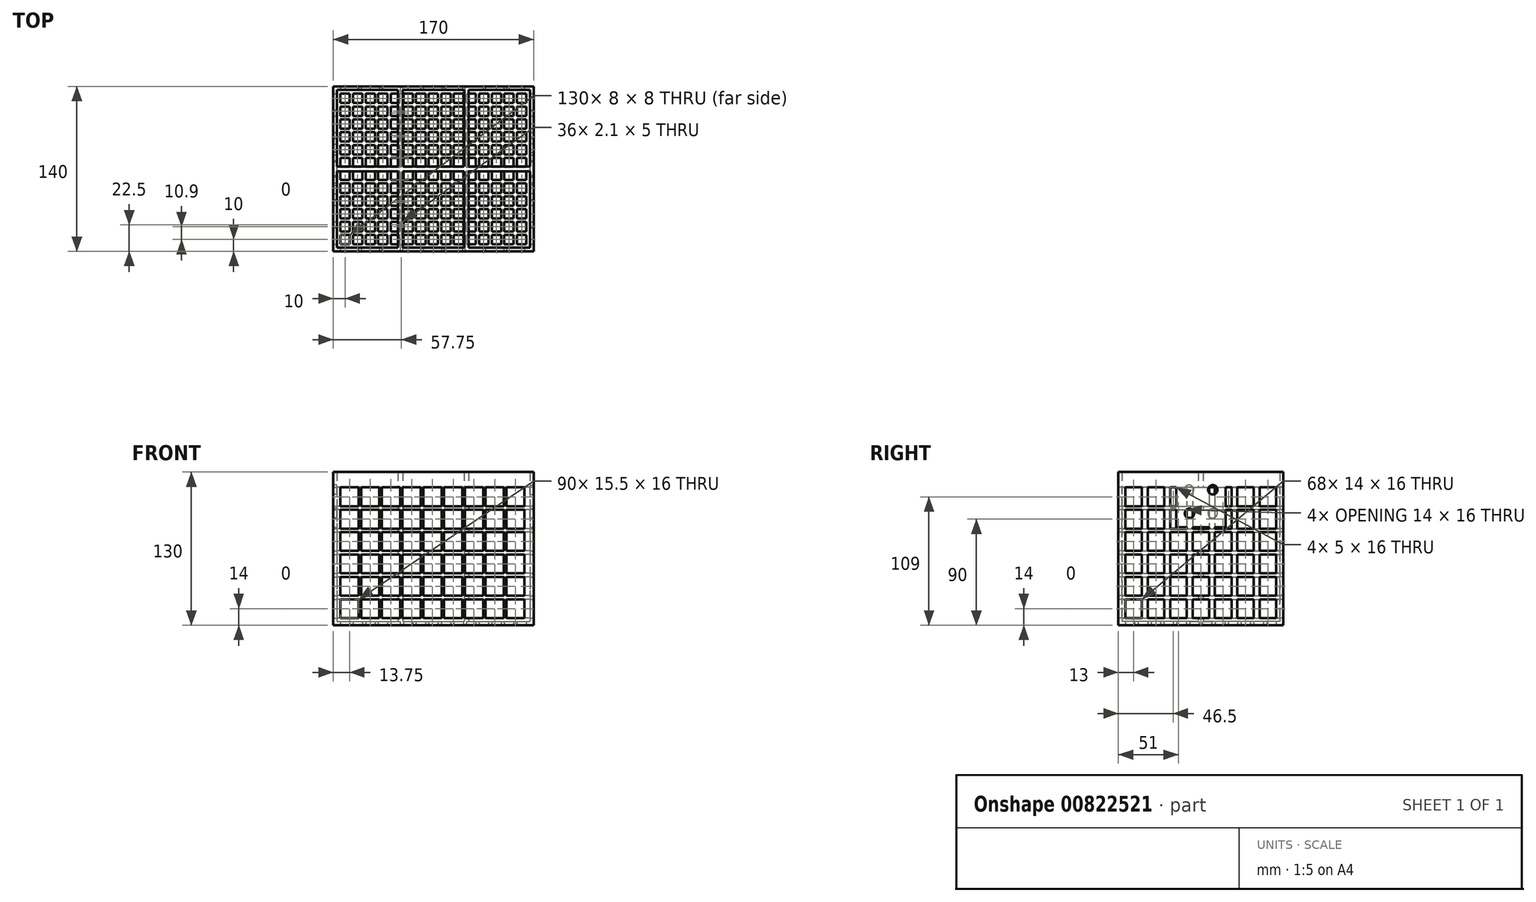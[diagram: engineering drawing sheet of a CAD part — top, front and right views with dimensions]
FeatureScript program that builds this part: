
annotation { "Feature Type Name" : "Feature", "Feature Type Description" : "" }
export const myFeature = defineFeature(function(context is Context, id is Id, definition is map)
    precondition{}
    {
        {
            var Q0;
            Q0=qCreatedBy(makeId("Top.planeOp"),FACE);
            var sketch = newSketch(context, id + "F0", { "sketchPlane" : qUnion([Q0])});
            skLineSegment(sketch, "E0.bottom", {"start": v(0, 0) * mm, "end": v(170, 0) * mm});
            skLineSegment(sketch, "E0.top", {"start": v(0, 140) * mm, "end": v(170, 140) * mm});
            skLineSegment(sketch, "E0.left", {"start": v(0, 0) * mm, "end": v(0, 140) * mm});
            skLineSegment(sketch, "E0.right", {"start": v(170, 0) * mm, "end": v(170, 140) * mm});
            skSolve(sketch);
        }
        {
            var Q0;
            Q0=qSketchRegion(id+"F0",true);
            extrude(context, id + "F1", {"entities" : qUnion([Q0]), "depth" : 130 * mm, "offsetDistance" : 25 * mm});
        }
        {
            var Q0;
            Q0=qCreatedBy(makeId("Top.planeOp"),FACE);
            cPlane(context, id + "F2", {"entities" : qUnion([Q0]), "cplaneType" : CPlaneType.OFFSET, "offset" : 3 * mm, "width" : 150 * mm, "height" : 150 * mm});
        }
        {
            var Q0;
            Q0=qCreatedBy(id+"F2.planeOp",FACE);
            var sketch = newSketch(context, id + "F3", { "sketchPlane" : qUnion([Q0])});
            skLineSegment(sketch, "E1.bottom", {"start": v(3, 68) * mm, "end": v(55, 68) * mm});
            skLineSegment(sketch, "E1.top", {"start": v(3, 3) * mm, "end": v(55, 3) * mm});
            skLineSegment(sketch, "E1.left", {"start": v(3, 68) * mm, "end": v(3, 3) * mm});
            skLineSegment(sketch, "E1.right", {"start": v(55, 68) * mm, "end": v(55, 3) * mm});
            skLineSegment(sketch, "E2", {"start": v(0, 137) * mm, "end": v(173.16, 137) * mm, "construction": true});
            skLineSegment(sketch, "E3", {"start": v(167, 0) * mm, "end": v(167, 146.13) * mm, "construction": true});
            skLineSegment(sketch, "E4.0.1.0", {"start": v(3, 137) * mm, "end": v(55, 137) * mm});
            skLineSegment(sketch, "E4.0.1.1", {"start": v(55, 137) * mm, "end": v(55, 72) * mm});
            skLineSegment(sketch, "E4.0.1.2", {"start": v(3, 72) * mm, "end": v(55, 72) * mm});
            skLineSegment(sketch, "E4.0.1.3", {"start": v(3, 137) * mm, "end": v(3, 72) * mm});
            skLineSegment(sketch, "E4.1.0.0", {"start": v(59, 68) * mm, "end": v(111, 68) * mm});
            skLineSegment(sketch, "E4.1.0.1", {"start": v(111, 68) * mm, "end": v(111, 3) * mm});
            skLineSegment(sketch, "E4.1.0.2", {"start": v(59, 3) * mm, "end": v(111, 3) * mm});
            skLineSegment(sketch, "E4.1.0.3", {"start": v(59, 68) * mm, "end": v(59, 3) * mm});
            skLineSegment(sketch, "E4.1.1.0", {"start": v(59, 137) * mm, "end": v(111, 137) * mm});
            skLineSegment(sketch, "E4.1.1.1", {"start": v(111, 137) * mm, "end": v(111, 72) * mm});
            skLineSegment(sketch, "E4.1.1.2", {"start": v(59, 72) * mm, "end": v(111, 72) * mm});
            skLineSegment(sketch, "E4.1.1.3", {"start": v(59, 137) * mm, "end": v(59, 72) * mm});
            skLineSegment(sketch, "E4.2.0.0", {"start": v(115, 68) * mm, "end": v(167, 68) * mm});
            skLineSegment(sketch, "E4.2.0.1", {"start": v(167, 68) * mm, "end": v(167, 3) * mm});
            skLineSegment(sketch, "E4.2.0.2", {"start": v(115, 3) * mm, "end": v(167, 3) * mm});
            skLineSegment(sketch, "E4.2.0.3", {"start": v(115, 68) * mm, "end": v(115, 3) * mm});
            skLineSegment(sketch, "E4.2.1.0", {"start": v(115, 137) * mm, "end": v(167, 137) * mm});
            skLineSegment(sketch, "E4.2.1.1", {"start": v(167, 137) * mm, "end": v(167, 72) * mm});
            skLineSegment(sketch, "E4.2.1.2", {"start": v(115, 72) * mm, "end": v(167, 72) * mm});
            skLineSegment(sketch, "E4.2.1.3", {"start": v(115, 137) * mm, "end": v(115, 72) * mm});
            skLineSegment(sketch, "E4.direction1", {"start": v(3, 3) * mm, "end": v(59, 3) * mm, "construction": true});
            skLineSegment(sketch, "E4.direction2", {"start": v(3, 3) * mm, "end": v(3, 72) * mm, "construction": true});
            skSolve(sketch);
        }
        {
            var Q0;
            Q0=qSketchRegion(id+"F3",true);
            extrude(context, id + "F4", {"entities" : qUnion([Q0]), "operationType" : NewBodyOperationType.REMOVE, "endBound" : BoundingType.UP_TO_NEXT, "depth" : 25 * mm, "offsetDistance" : 25 * mm});
        }
        {
            var Q0;
            Q0=qCreatedBy(makeId("Top.planeOp"),FACE);
            var sketch = newSketch(context, id + "F5", { "sketchPlane" : qUnion([Q0])});
            skLineSegment(sketch, "E5.bottom", {"start": v(6, 6) * mm, "end": v(14, 6) * mm});
            skLineSegment(sketch, "E5.top", {"start": v(6, 14) * mm, "end": v(14, 14) * mm});
            skLineSegment(sketch, "E5.left", {"start": v(6, 6) * mm, "end": v(6, 14) * mm});
            skLineSegment(sketch, "E5.right", {"start": v(14, 6) * mm, "end": v(14, 14) * mm});
            skLineSegment(sketch, "E6", {"start": v(164, 0) * mm, "end": v(164, 62.65) * mm, "construction": true});
            skLineSegment(sketch, "E7", {"start": v(-7.34, 134) * mm, "end": v(91.38, 134) * mm, "construction": true});
            skLineSegment(sketch, "E8.0.1.0", {"start": v(6, 16.9) * mm, "end": v(14, 16.9) * mm});
            skLineSegment(sketch, "E8.0.1.1", {"start": v(14, 16.9) * mm, "end": v(14, 24.9) * mm});
            skLineSegment(sketch, "E8.0.1.2", {"start": v(6, 24.9) * mm, "end": v(14, 24.9) * mm});
            skLineSegment(sketch, "E8.0.1.3", {"start": v(6, 16.9) * mm, "end": v(6, 24.9) * mm});
            skLineSegment(sketch, "E8.0.2.0", {"start": v(6, 27.8) * mm, "end": v(14, 27.8) * mm});
            skLineSegment(sketch, "E8.0.2.1", {"start": v(14, 27.8) * mm, "end": v(14, 35.8) * mm});
            skLineSegment(sketch, "E8.0.2.2", {"start": v(6, 35.8) * mm, "end": v(14, 35.8) * mm});
            skLineSegment(sketch, "E8.0.2.3", {"start": v(6, 27.8) * mm, "end": v(6, 35.8) * mm});
            skLineSegment(sketch, "E8.0.3.0", {"start": v(6, 38.7) * mm, "end": v(14, 38.7) * mm});
            skLineSegment(sketch, "E8.0.3.1", {"start": v(14, 38.7) * mm, "end": v(14, 46.7) * mm});
            skLineSegment(sketch, "E8.0.3.2", {"start": v(6, 46.7) * mm, "end": v(14, 46.7) * mm});
            skLineSegment(sketch, "E8.0.3.3", {"start": v(6, 38.7) * mm, "end": v(6, 46.7) * mm});
            skLineSegment(sketch, "E8.0.4.0", {"start": v(6, 49.6) * mm, "end": v(14, 49.6) * mm});
            skLineSegment(sketch, "E8.0.4.1", {"start": v(14, 49.6) * mm, "end": v(14, 57.6) * mm});
            skLineSegment(sketch, "E8.0.4.2", {"start": v(6, 57.6) * mm, "end": v(14, 57.6) * mm});
            skLineSegment(sketch, "E8.0.4.3", {"start": v(6, 49.6) * mm, "end": v(6, 57.6) * mm});
            skLineSegment(sketch, "E8.0.5.0", {"start": v(6, 60.5) * mm, "end": v(14, 60.5) * mm});
            skLineSegment(sketch, "E8.0.5.1", {"start": v(14, 60.5) * mm, "end": v(14, 68.5) * mm});
            skLineSegment(sketch, "E8.0.5.2", {"start": v(6, 68.5) * mm, "end": v(14, 68.5) * mm});
            skLineSegment(sketch, "E8.0.5.3", {"start": v(6, 60.5) * mm, "end": v(6, 68.5) * mm});
            skLineSegment(sketch, "E8.0.6.0", {"start": v(6, 71.4) * mm, "end": v(14, 71.4) * mm});
            skLineSegment(sketch, "E8.0.6.1", {"start": v(14, 71.4) * mm, "end": v(14, 79.4) * mm});
            skLineSegment(sketch, "E8.0.6.2", {"start": v(6, 79.4) * mm, "end": v(14, 79.4) * mm});
            skLineSegment(sketch, "E8.0.6.3", {"start": v(6, 71.4) * mm, "end": v(6, 79.4) * mm});
            skLineSegment(sketch, "E8.0.7.0", {"start": v(6, 82.3) * mm, "end": v(14, 82.3) * mm});
            skLineSegment(sketch, "E8.0.7.1", {"start": v(14, 82.3) * mm, "end": v(14, 90.3) * mm});
            skLineSegment(sketch, "E8.0.7.2", {"start": v(6, 90.3) * mm, "end": v(14, 90.3) * mm});
            skLineSegment(sketch, "E8.0.7.3", {"start": v(6, 82.3) * mm, "end": v(6, 90.3) * mm});
            skLineSegment(sketch, "E8.0.8.0", {"start": v(6, 93.2) * mm, "end": v(14, 93.2) * mm});
            skLineSegment(sketch, "E8.0.8.1", {"start": v(14, 93.2) * mm, "end": v(14, 101.2) * mm});
            skLineSegment(sketch, "E8.0.8.2", {"start": v(6, 101.2) * mm, "end": v(14, 101.2) * mm});
            skLineSegment(sketch, "E8.0.8.3", {"start": v(6, 93.2) * mm, "end": v(6, 101.2) * mm});
            skLineSegment(sketch, "E8.0.9.0", {"start": v(6, 104.1) * mm, "end": v(14, 104.1) * mm});
            skLineSegment(sketch, "E8.0.9.1", {"start": v(14, 104.1) * mm, "end": v(14, 112.1) * mm});
            skLineSegment(sketch, "E8.0.9.2", {"start": v(6, 112.1) * mm, "end": v(14, 112.1) * mm});
            skLineSegment(sketch, "E8.0.9.3", {"start": v(6, 104.1) * mm, "end": v(6, 112.1) * mm});
            skLineSegment(sketch, "E8.0.10.0", {"start": v(6, 115) * mm, "end": v(14, 115) * mm});
            skLineSegment(sketch, "E8.0.10.1", {"start": v(14, 115) * mm, "end": v(14, 123) * mm});
            skLineSegment(sketch, "E8.0.10.2", {"start": v(6, 123) * mm, "end": v(14, 123) * mm});
            skLineSegment(sketch, "E8.0.10.3", {"start": v(6, 115) * mm, "end": v(6, 123) * mm});
            skLineSegment(sketch, "E8.0.11.0", {"start": v(6, 125.9) * mm, "end": v(14, 125.9) * mm});
            skLineSegment(sketch, "E8.0.11.1", {"start": v(14, 125.9) * mm, "end": v(14, 133.9) * mm});
            skLineSegment(sketch, "E8.0.11.2", {"start": v(6, 133.9) * mm, "end": v(14, 133.9) * mm});
            skLineSegment(sketch, "E8.0.11.3", {"start": v(6, 125.9) * mm, "end": v(6, 133.9) * mm});
            skLineSegment(sketch, "E8.1.0.0", {"start": v(16.7, 6) * mm, "end": v(24.7, 6) * mm});
            skLineSegment(sketch, "E8.1.0.1", {"start": v(24.7, 6) * mm, "end": v(24.7, 14) * mm});
            skLineSegment(sketch, "E8.1.0.2", {"start": v(16.7, 14) * mm, "end": v(24.7, 14) * mm});
            skLineSegment(sketch, "E8.1.0.3", {"start": v(16.7, 6) * mm, "end": v(16.7, 14) * mm});
            skLineSegment(sketch, "E8.1.1.0", {"start": v(16.7, 16.9) * mm, "end": v(24.7, 16.9) * mm});
            skLineSegment(sketch, "E8.1.1.1", {"start": v(24.7, 16.9) * mm, "end": v(24.7, 24.9) * mm});
            skLineSegment(sketch, "E8.1.1.2", {"start": v(16.7, 24.9) * mm, "end": v(24.7, 24.9) * mm});
            skLineSegment(sketch, "E8.1.1.3", {"start": v(16.7, 16.9) * mm, "end": v(16.7, 24.9) * mm});
            skLineSegment(sketch, "E8.1.2.0", {"start": v(16.7, 27.8) * mm, "end": v(24.7, 27.8) * mm});
            skLineSegment(sketch, "E8.1.2.1", {"start": v(24.7, 27.8) * mm, "end": v(24.7, 35.8) * mm});
            skLineSegment(sketch, "E8.1.2.2", {"start": v(16.7, 35.8) * mm, "end": v(24.7, 35.8) * mm});
            skLineSegment(sketch, "E8.1.2.3", {"start": v(16.7, 27.8) * mm, "end": v(16.7, 35.8) * mm});
            skLineSegment(sketch, "E8.1.3.0", {"start": v(16.7, 38.7) * mm, "end": v(24.7, 38.7) * mm});
            skLineSegment(sketch, "E8.1.3.1", {"start": v(24.7, 38.7) * mm, "end": v(24.7, 46.7) * mm});
            skLineSegment(sketch, "E8.1.3.2", {"start": v(16.7, 46.7) * mm, "end": v(24.7, 46.7) * mm});
            skLineSegment(sketch, "E8.1.3.3", {"start": v(16.7, 38.7) * mm, "end": v(16.7, 46.7) * mm});
            skLineSegment(sketch, "E8.1.4.0", {"start": v(16.7, 49.6) * mm, "end": v(24.7, 49.6) * mm});
            skLineSegment(sketch, "E8.1.4.1", {"start": v(24.7, 49.6) * mm, "end": v(24.7, 57.6) * mm});
            skLineSegment(sketch, "E8.1.4.2", {"start": v(16.7, 57.6) * mm, "end": v(24.7, 57.6) * mm});
            skLineSegment(sketch, "E8.1.4.3", {"start": v(16.7, 49.6) * mm, "end": v(16.7, 57.6) * mm});
            skLineSegment(sketch, "E8.1.5.0", {"start": v(16.7, 60.5) * mm, "end": v(24.7, 60.5) * mm});
            skLineSegment(sketch, "E8.1.5.1", {"start": v(24.7, 60.5) * mm, "end": v(24.7, 68.5) * mm});
            skLineSegment(sketch, "E8.1.5.2", {"start": v(16.7, 68.5) * mm, "end": v(24.7, 68.5) * mm});
            skLineSegment(sketch, "E8.1.5.3", {"start": v(16.7, 60.5) * mm, "end": v(16.7, 68.5) * mm});
            skLineSegment(sketch, "E8.1.6.0", {"start": v(16.7, 71.4) * mm, "end": v(24.7, 71.4) * mm});
            skLineSegment(sketch, "E8.1.6.1", {"start": v(24.7, 71.4) * mm, "end": v(24.7, 79.4) * mm});
            skLineSegment(sketch, "E8.1.6.2", {"start": v(16.7, 79.4) * mm, "end": v(24.7, 79.4) * mm});
            skLineSegment(sketch, "E8.1.6.3", {"start": v(16.7, 71.4) * mm, "end": v(16.7, 79.4) * mm});
            skLineSegment(sketch, "E8.1.7.0", {"start": v(16.7, 82.3) * mm, "end": v(24.7, 82.3) * mm});
            skLineSegment(sketch, "E8.1.7.1", {"start": v(24.7, 82.3) * mm, "end": v(24.7, 90.3) * mm});
            skLineSegment(sketch, "E8.1.7.2", {"start": v(16.7, 90.3) * mm, "end": v(24.7, 90.3) * mm});
            skLineSegment(sketch, "E8.1.7.3", {"start": v(16.7, 82.3) * mm, "end": v(16.7, 90.3) * mm});
            skLineSegment(sketch, "E8.1.8.0", {"start": v(16.7, 93.2) * mm, "end": v(24.7, 93.2) * mm});
            skLineSegment(sketch, "E8.1.8.1", {"start": v(24.7, 93.2) * mm, "end": v(24.7, 101.2) * mm});
            skLineSegment(sketch, "E8.1.8.2", {"start": v(16.7, 101.2) * mm, "end": v(24.7, 101.2) * mm});
            skLineSegment(sketch, "E8.1.8.3", {"start": v(16.7, 93.2) * mm, "end": v(16.7, 101.2) * mm});
            skLineSegment(sketch, "E8.1.9.0", {"start": v(16.7, 104.1) * mm, "end": v(24.7, 104.1) * mm});
            skLineSegment(sketch, "E8.1.9.1", {"start": v(24.7, 104.1) * mm, "end": v(24.7, 112.1) * mm});
            skLineSegment(sketch, "E8.1.9.2", {"start": v(16.7, 112.1) * mm, "end": v(24.7, 112.1) * mm});
            skLineSegment(sketch, "E8.1.9.3", {"start": v(16.7, 104.1) * mm, "end": v(16.7, 112.1) * mm});
            skLineSegment(sketch, "E8.1.10.0", {"start": v(16.7, 115) * mm, "end": v(24.7, 115) * mm});
            skLineSegment(sketch, "E8.1.10.1", {"start": v(24.7, 115) * mm, "end": v(24.7, 123) * mm});
            skLineSegment(sketch, "E8.1.10.2", {"start": v(16.7, 123) * mm, "end": v(24.7, 123) * mm});
            skLineSegment(sketch, "E8.1.10.3", {"start": v(16.7, 115) * mm, "end": v(16.7, 123) * mm});
            skLineSegment(sketch, "E8.1.11.0", {"start": v(16.7, 125.9) * mm, "end": v(24.7, 125.9) * mm});
            skLineSegment(sketch, "E8.1.11.1", {"start": v(24.7, 125.9) * mm, "end": v(24.7, 133.9) * mm});
            skLineSegment(sketch, "E8.1.11.2", {"start": v(16.7, 133.9) * mm, "end": v(24.7, 133.9) * mm});
            skLineSegment(sketch, "E8.1.11.3", {"start": v(16.7, 125.9) * mm, "end": v(16.7, 133.9) * mm});
            skLineSegment(sketch, "E8.2.0.0", {"start": v(27.4, 6) * mm, "end": v(35.4, 6) * mm});
            skLineSegment(sketch, "E8.2.0.1", {"start": v(35.4, 6) * mm, "end": v(35.4, 14) * mm});
            skLineSegment(sketch, "E8.2.0.2", {"start": v(27.4, 14) * mm, "end": v(35.4, 14) * mm});
            skLineSegment(sketch, "E8.2.0.3", {"start": v(27.4, 6) * mm, "end": v(27.4, 14) * mm});
            skLineSegment(sketch, "E8.2.1.0", {"start": v(27.4, 16.9) * mm, "end": v(35.4, 16.9) * mm});
            skLineSegment(sketch, "E8.2.1.1", {"start": v(35.4, 16.9) * mm, "end": v(35.4, 24.9) * mm});
            skLineSegment(sketch, "E8.2.1.2", {"start": v(27.4, 24.9) * mm, "end": v(35.4, 24.9) * mm});
            skLineSegment(sketch, "E8.2.1.3", {"start": v(27.4, 16.9) * mm, "end": v(27.4, 24.9) * mm});
            skLineSegment(sketch, "E8.2.2.0", {"start": v(27.4, 27.8) * mm, "end": v(35.4, 27.8) * mm});
            skLineSegment(sketch, "E8.2.2.1", {"start": v(35.4, 27.8) * mm, "end": v(35.4, 35.8) * mm});
            skLineSegment(sketch, "E8.2.2.2", {"start": v(27.4, 35.8) * mm, "end": v(35.4, 35.8) * mm});
            skLineSegment(sketch, "E8.2.2.3", {"start": v(27.4, 27.8) * mm, "end": v(27.4, 35.8) * mm});
            skLineSegment(sketch, "E8.2.3.0", {"start": v(27.4, 38.7) * mm, "end": v(35.4, 38.7) * mm});
            skLineSegment(sketch, "E8.2.3.1", {"start": v(35.4, 38.7) * mm, "end": v(35.4, 46.7) * mm});
            skLineSegment(sketch, "E8.2.3.2", {"start": v(27.4, 46.7) * mm, "end": v(35.4, 46.7) * mm});
            skLineSegment(sketch, "E8.2.3.3", {"start": v(27.4, 38.7) * mm, "end": v(27.4, 46.7) * mm});
            skLineSegment(sketch, "E8.2.4.0", {"start": v(27.4, 49.6) * mm, "end": v(35.4, 49.6) * mm});
            skLineSegment(sketch, "E8.2.4.1", {"start": v(35.4, 49.6) * mm, "end": v(35.4, 57.6) * mm});
            skLineSegment(sketch, "E8.2.4.2", {"start": v(27.4, 57.6) * mm, "end": v(35.4, 57.6) * mm});
            skLineSegment(sketch, "E8.2.4.3", {"start": v(27.4, 49.6) * mm, "end": v(27.4, 57.6) * mm});
            skLineSegment(sketch, "E8.2.5.0", {"start": v(27.4, 60.5) * mm, "end": v(35.4, 60.5) * mm});
            skLineSegment(sketch, "E8.2.5.1", {"start": v(35.4, 60.5) * mm, "end": v(35.4, 68.5) * mm});
            skLineSegment(sketch, "E8.2.5.2", {"start": v(27.4, 68.5) * mm, "end": v(35.4, 68.5) * mm});
            skLineSegment(sketch, "E8.2.5.3", {"start": v(27.4, 60.5) * mm, "end": v(27.4, 68.5) * mm});
            skLineSegment(sketch, "E8.2.6.0", {"start": v(27.4, 71.4) * mm, "end": v(35.4, 71.4) * mm});
            skLineSegment(sketch, "E8.2.6.1", {"start": v(35.4, 71.4) * mm, "end": v(35.4, 79.4) * mm});
            skLineSegment(sketch, "E8.2.6.2", {"start": v(27.4, 79.4) * mm, "end": v(35.4, 79.4) * mm});
            skLineSegment(sketch, "E8.2.6.3", {"start": v(27.4, 71.4) * mm, "end": v(27.4, 79.4) * mm});
            skLineSegment(sketch, "E8.2.7.0", {"start": v(27.4, 82.3) * mm, "end": v(35.4, 82.3) * mm});
            skLineSegment(sketch, "E8.2.7.1", {"start": v(35.4, 82.3) * mm, "end": v(35.4, 90.3) * mm});
            skLineSegment(sketch, "E8.2.7.2", {"start": v(27.4, 90.3) * mm, "end": v(35.4, 90.3) * mm});
            skLineSegment(sketch, "E8.2.7.3", {"start": v(27.4, 82.3) * mm, "end": v(27.4, 90.3) * mm});
            skLineSegment(sketch, "E8.2.8.0", {"start": v(27.4, 93.2) * mm, "end": v(35.4, 93.2) * mm});
            skLineSegment(sketch, "E8.2.8.1", {"start": v(35.4, 93.2) * mm, "end": v(35.4, 101.2) * mm});
            skLineSegment(sketch, "E8.2.8.2", {"start": v(27.4, 101.2) * mm, "end": v(35.4, 101.2) * mm});
            skLineSegment(sketch, "E8.2.8.3", {"start": v(27.4, 93.2) * mm, "end": v(27.4, 101.2) * mm});
            skLineSegment(sketch, "E8.2.9.0", {"start": v(27.4, 104.1) * mm, "end": v(35.4, 104.1) * mm});
            skLineSegment(sketch, "E8.2.9.1", {"start": v(35.4, 104.1) * mm, "end": v(35.4, 112.1) * mm});
            skLineSegment(sketch, "E8.2.9.2", {"start": v(27.4, 112.1) * mm, "end": v(35.4, 112.1) * mm});
            skLineSegment(sketch, "E8.2.9.3", {"start": v(27.4, 104.1) * mm, "end": v(27.4, 112.1) * mm});
            skLineSegment(sketch, "E8.2.10.0", {"start": v(27.4, 115) * mm, "end": v(35.4, 115) * mm});
            skLineSegment(sketch, "E8.2.10.1", {"start": v(35.4, 115) * mm, "end": v(35.4, 123) * mm});
            skLineSegment(sketch, "E8.2.10.2", {"start": v(27.4, 123) * mm, "end": v(35.4, 123) * mm});
            skLineSegment(sketch, "E8.2.10.3", {"start": v(27.4, 115) * mm, "end": v(27.4, 123) * mm});
            skLineSegment(sketch, "E8.2.11.0", {"start": v(27.4, 125.9) * mm, "end": v(35.4, 125.9) * mm});
            skLineSegment(sketch, "E8.2.11.1", {"start": v(35.4, 125.9) * mm, "end": v(35.4, 133.9) * mm});
            skLineSegment(sketch, "E8.2.11.2", {"start": v(27.4, 133.9) * mm, "end": v(35.4, 133.9) * mm});
            skLineSegment(sketch, "E8.2.11.3", {"start": v(27.4, 125.9) * mm, "end": v(27.4, 133.9) * mm});
            skLineSegment(sketch, "E8.3.0.0", {"start": v(38.1, 6) * mm, "end": v(46.1, 6) * mm});
            skLineSegment(sketch, "E8.3.0.1", {"start": v(46.1, 6) * mm, "end": v(46.1, 14) * mm});
            skLineSegment(sketch, "E8.3.0.2", {"start": v(38.1, 14) * mm, "end": v(46.1, 14) * mm});
            skLineSegment(sketch, "E8.3.0.3", {"start": v(38.1, 6) * mm, "end": v(38.1, 14) * mm});
            skLineSegment(sketch, "E8.3.1.0", {"start": v(38.1, 16.9) * mm, "end": v(46.1, 16.9) * mm});
            skLineSegment(sketch, "E8.3.1.1", {"start": v(46.1, 16.9) * mm, "end": v(46.1, 24.9) * mm});
            skLineSegment(sketch, "E8.3.1.2", {"start": v(38.1, 24.9) * mm, "end": v(46.1, 24.9) * mm});
            skLineSegment(sketch, "E8.3.1.3", {"start": v(38.1, 16.9) * mm, "end": v(38.1, 24.9) * mm});
            skLineSegment(sketch, "E8.3.2.0", {"start": v(38.1, 27.8) * mm, "end": v(46.1, 27.8) * mm});
            skLineSegment(sketch, "E8.3.2.1", {"start": v(46.1, 27.8) * mm, "end": v(46.1, 35.8) * mm});
            skLineSegment(sketch, "E8.3.2.2", {"start": v(38.1, 35.8) * mm, "end": v(46.1, 35.8) * mm});
            skLineSegment(sketch, "E8.3.2.3", {"start": v(38.1, 27.8) * mm, "end": v(38.1, 35.8) * mm});
            skLineSegment(sketch, "E8.3.3.0", {"start": v(38.1, 38.7) * mm, "end": v(46.1, 38.7) * mm});
            skLineSegment(sketch, "E8.3.3.1", {"start": v(46.1, 38.7) * mm, "end": v(46.1, 46.7) * mm});
            skLineSegment(sketch, "E8.3.3.2", {"start": v(38.1, 46.7) * mm, "end": v(46.1, 46.7) * mm});
            skLineSegment(sketch, "E8.3.3.3", {"start": v(38.1, 38.7) * mm, "end": v(38.1, 46.7) * mm});
            skLineSegment(sketch, "E8.3.4.0", {"start": v(38.1, 49.6) * mm, "end": v(46.1, 49.6) * mm});
            skLineSegment(sketch, "E8.3.4.1", {"start": v(46.1, 49.6) * mm, "end": v(46.1, 57.6) * mm});
            skLineSegment(sketch, "E8.3.4.2", {"start": v(38.1, 57.6) * mm, "end": v(46.1, 57.6) * mm});
            skLineSegment(sketch, "E8.3.4.3", {"start": v(38.1, 49.6) * mm, "end": v(38.1, 57.6) * mm});
            skLineSegment(sketch, "E8.3.5.0", {"start": v(38.1, 60.5) * mm, "end": v(46.1, 60.5) * mm});
            skLineSegment(sketch, "E8.3.5.1", {"start": v(46.1, 60.5) * mm, "end": v(46.1, 68.5) * mm});
            skLineSegment(sketch, "E8.3.5.2", {"start": v(38.1, 68.5) * mm, "end": v(46.1, 68.5) * mm});
            skLineSegment(sketch, "E8.3.5.3", {"start": v(38.1, 60.5) * mm, "end": v(38.1, 68.5) * mm});
            skLineSegment(sketch, "E8.3.6.0", {"start": v(38.1, 71.4) * mm, "end": v(46.1, 71.4) * mm});
            skLineSegment(sketch, "E8.3.6.1", {"start": v(46.1, 71.4) * mm, "end": v(46.1, 79.4) * mm});
            skLineSegment(sketch, "E8.3.6.2", {"start": v(38.1, 79.4) * mm, "end": v(46.1, 79.4) * mm});
            skLineSegment(sketch, "E8.3.6.3", {"start": v(38.1, 71.4) * mm, "end": v(38.1, 79.4) * mm});
            skLineSegment(sketch, "E8.3.7.0", {"start": v(38.1, 82.3) * mm, "end": v(46.1, 82.3) * mm});
            skLineSegment(sketch, "E8.3.7.1", {"start": v(46.1, 82.3) * mm, "end": v(46.1, 90.3) * mm});
            skLineSegment(sketch, "E8.3.7.2", {"start": v(38.1, 90.3) * mm, "end": v(46.1, 90.3) * mm});
            skLineSegment(sketch, "E8.3.7.3", {"start": v(38.1, 82.3) * mm, "end": v(38.1, 90.3) * mm});
            skLineSegment(sketch, "E8.3.8.0", {"start": v(38.1, 93.2) * mm, "end": v(46.1, 93.2) * mm});
            skLineSegment(sketch, "E8.3.8.1", {"start": v(46.1, 93.2) * mm, "end": v(46.1, 101.2) * mm});
            skLineSegment(sketch, "E8.3.8.2", {"start": v(38.1, 101.2) * mm, "end": v(46.1, 101.2) * mm});
            skLineSegment(sketch, "E8.3.8.3", {"start": v(38.1, 93.2) * mm, "end": v(38.1, 101.2) * mm});
            skLineSegment(sketch, "E8.3.9.0", {"start": v(38.1, 104.1) * mm, "end": v(46.1, 104.1) * mm});
            skLineSegment(sketch, "E8.3.9.1", {"start": v(46.1, 104.1) * mm, "end": v(46.1, 112.1) * mm});
            skLineSegment(sketch, "E8.3.9.2", {"start": v(38.1, 112.1) * mm, "end": v(46.1, 112.1) * mm});
            skLineSegment(sketch, "E8.3.9.3", {"start": v(38.1, 104.1) * mm, "end": v(38.1, 112.1) * mm});
            skLineSegment(sketch, "E8.3.10.0", {"start": v(38.1, 115) * mm, "end": v(46.1, 115) * mm});
            skLineSegment(sketch, "E8.3.10.1", {"start": v(46.1, 115) * mm, "end": v(46.1, 123) * mm});
            skLineSegment(sketch, "E8.3.10.2", {"start": v(38.1, 123) * mm, "end": v(46.1, 123) * mm});
            skLineSegment(sketch, "E8.3.10.3", {"start": v(38.1, 115) * mm, "end": v(38.1, 123) * mm});
            skLineSegment(sketch, "E8.3.11.0", {"start": v(38.1, 125.9) * mm, "end": v(46.1, 125.9) * mm});
            skLineSegment(sketch, "E8.3.11.1", {"start": v(46.1, 125.9) * mm, "end": v(46.1, 133.9) * mm});
            skLineSegment(sketch, "E8.3.11.2", {"start": v(38.1, 133.9) * mm, "end": v(46.1, 133.9) * mm});
            skLineSegment(sketch, "E8.3.11.3", {"start": v(38.1, 125.9) * mm, "end": v(38.1, 133.9) * mm});
            skLineSegment(sketch, "E8.4.0.0", {"start": v(48.8, 6) * mm, "end": v(56.8, 6) * mm});
            skLineSegment(sketch, "E8.4.0.1", {"start": v(56.8, 6) * mm, "end": v(56.8, 14) * mm});
            skLineSegment(sketch, "E8.4.0.2", {"start": v(48.8, 14) * mm, "end": v(56.8, 14) * mm});
            skLineSegment(sketch, "E8.4.0.3", {"start": v(48.8, 6) * mm, "end": v(48.8, 14) * mm});
            skLineSegment(sketch, "E8.4.1.0", {"start": v(48.8, 16.9) * mm, "end": v(56.8, 16.9) * mm});
            skLineSegment(sketch, "E8.4.1.1", {"start": v(56.8, 16.9) * mm, "end": v(56.8, 24.9) * mm});
            skLineSegment(sketch, "E8.4.1.2", {"start": v(48.8, 24.9) * mm, "end": v(56.8, 24.9) * mm});
            skLineSegment(sketch, "E8.4.1.3", {"start": v(48.8, 16.9) * mm, "end": v(48.8, 24.9) * mm});
            skLineSegment(sketch, "E8.4.2.0", {"start": v(48.8, 27.8) * mm, "end": v(56.8, 27.8) * mm});
            skLineSegment(sketch, "E8.4.2.1", {"start": v(56.8, 27.8) * mm, "end": v(56.8, 35.8) * mm});
            skLineSegment(sketch, "E8.4.2.2", {"start": v(48.8, 35.8) * mm, "end": v(56.8, 35.8) * mm});
            skLineSegment(sketch, "E8.4.2.3", {"start": v(48.8, 27.8) * mm, "end": v(48.8, 35.8) * mm});
            skLineSegment(sketch, "E8.4.3.0", {"start": v(48.8, 38.7) * mm, "end": v(56.8, 38.7) * mm});
            skLineSegment(sketch, "E8.4.3.1", {"start": v(56.8, 38.7) * mm, "end": v(56.8, 46.7) * mm});
            skLineSegment(sketch, "E8.4.3.2", {"start": v(48.8, 46.7) * mm, "end": v(56.8, 46.7) * mm});
            skLineSegment(sketch, "E8.4.3.3", {"start": v(48.8, 38.7) * mm, "end": v(48.8, 46.7) * mm});
            skLineSegment(sketch, "E8.4.4.0", {"start": v(48.8, 49.6) * mm, "end": v(56.8, 49.6) * mm});
            skLineSegment(sketch, "E8.4.4.1", {"start": v(56.8, 49.6) * mm, "end": v(56.8, 57.6) * mm});
            skLineSegment(sketch, "E8.4.4.2", {"start": v(48.8, 57.6) * mm, "end": v(56.8, 57.6) * mm});
            skLineSegment(sketch, "E8.4.4.3", {"start": v(48.8, 49.6) * mm, "end": v(48.8, 57.6) * mm});
            skLineSegment(sketch, "E8.4.5.0", {"start": v(48.8, 60.5) * mm, "end": v(56.8, 60.5) * mm});
            skLineSegment(sketch, "E8.4.5.1", {"start": v(56.8, 60.5) * mm, "end": v(56.8, 68.5) * mm});
            skLineSegment(sketch, "E8.4.5.2", {"start": v(48.8, 68.5) * mm, "end": v(56.8, 68.5) * mm});
            skLineSegment(sketch, "E8.4.5.3", {"start": v(48.8, 60.5) * mm, "end": v(48.8, 68.5) * mm});
            skLineSegment(sketch, "E8.4.6.0", {"start": v(48.8, 71.4) * mm, "end": v(56.8, 71.4) * mm});
            skLineSegment(sketch, "E8.4.6.1", {"start": v(56.8, 71.4) * mm, "end": v(56.8, 79.4) * mm});
            skLineSegment(sketch, "E8.4.6.2", {"start": v(48.8, 79.4) * mm, "end": v(56.8, 79.4) * mm});
            skLineSegment(sketch, "E8.4.6.3", {"start": v(48.8, 71.4) * mm, "end": v(48.8, 79.4) * mm});
            skLineSegment(sketch, "E8.4.7.0", {"start": v(48.8, 82.3) * mm, "end": v(56.8, 82.3) * mm});
            skLineSegment(sketch, "E8.4.7.1", {"start": v(56.8, 82.3) * mm, "end": v(56.8, 90.3) * mm});
            skLineSegment(sketch, "E8.4.7.2", {"start": v(48.8, 90.3) * mm, "end": v(56.8, 90.3) * mm});
            skLineSegment(sketch, "E8.4.7.3", {"start": v(48.8, 82.3) * mm, "end": v(48.8, 90.3) * mm});
            skLineSegment(sketch, "E8.4.8.0", {"start": v(48.8, 93.2) * mm, "end": v(56.8, 93.2) * mm});
            skLineSegment(sketch, "E8.4.8.1", {"start": v(56.8, 93.2) * mm, "end": v(56.8, 101.2) * mm});
            skLineSegment(sketch, "E8.4.8.2", {"start": v(48.8, 101.2) * mm, "end": v(56.8, 101.2) * mm});
            skLineSegment(sketch, "E8.4.8.3", {"start": v(48.8, 93.2) * mm, "end": v(48.8, 101.2) * mm});
            skLineSegment(sketch, "E8.4.9.0", {"start": v(48.8, 104.1) * mm, "end": v(56.8, 104.1) * mm});
            skLineSegment(sketch, "E8.4.9.1", {"start": v(56.8, 104.1) * mm, "end": v(56.8, 112.1) * mm});
            skLineSegment(sketch, "E8.4.9.2", {"start": v(48.8, 112.1) * mm, "end": v(56.8, 112.1) * mm});
            skLineSegment(sketch, "E8.4.9.3", {"start": v(48.8, 104.1) * mm, "end": v(48.8, 112.1) * mm});
            skLineSegment(sketch, "E8.4.10.0", {"start": v(48.8, 115) * mm, "end": v(56.8, 115) * mm});
            skLineSegment(sketch, "E8.4.10.1", {"start": v(56.8, 115) * mm, "end": v(56.8, 123) * mm});
            skLineSegment(sketch, "E8.4.10.2", {"start": v(48.8, 123) * mm, "end": v(56.8, 123) * mm});
            skLineSegment(sketch, "E8.4.10.3", {"start": v(48.8, 115) * mm, "end": v(48.8, 123) * mm});
            skLineSegment(sketch, "E8.4.11.0", {"start": v(48.8, 125.9) * mm, "end": v(56.8, 125.9) * mm});
            skLineSegment(sketch, "E8.4.11.1", {"start": v(56.8, 125.9) * mm, "end": v(56.8, 133.9) * mm});
            skLineSegment(sketch, "E8.4.11.2", {"start": v(48.8, 133.9) * mm, "end": v(56.8, 133.9) * mm});
            skLineSegment(sketch, "E8.4.11.3", {"start": v(48.8, 125.9) * mm, "end": v(48.8, 133.9) * mm});
            skLineSegment(sketch, "E8.5.0.0", {"start": v(59.5, 6) * mm, "end": v(67.5, 6) * mm});
            skLineSegment(sketch, "E8.5.0.1", {"start": v(67.5, 6) * mm, "end": v(67.5, 14) * mm});
            skLineSegment(sketch, "E8.5.0.2", {"start": v(59.5, 14) * mm, "end": v(67.5, 14) * mm});
            skLineSegment(sketch, "E8.5.0.3", {"start": v(59.5, 6) * mm, "end": v(59.5, 14) * mm});
            skLineSegment(sketch, "E8.5.1.0", {"start": v(59.5, 16.9) * mm, "end": v(67.5, 16.9) * mm});
            skLineSegment(sketch, "E8.5.1.1", {"start": v(67.5, 16.9) * mm, "end": v(67.5, 24.9) * mm});
            skLineSegment(sketch, "E8.5.1.2", {"start": v(59.5, 24.9) * mm, "end": v(67.5, 24.9) * mm});
            skLineSegment(sketch, "E8.5.1.3", {"start": v(59.5, 16.9) * mm, "end": v(59.5, 24.9) * mm});
            skLineSegment(sketch, "E8.5.2.0", {"start": v(59.5, 27.8) * mm, "end": v(67.5, 27.8) * mm});
            skLineSegment(sketch, "E8.5.2.1", {"start": v(67.5, 27.8) * mm, "end": v(67.5, 35.8) * mm});
            skLineSegment(sketch, "E8.5.2.2", {"start": v(59.5, 35.8) * mm, "end": v(67.5, 35.8) * mm});
            skLineSegment(sketch, "E8.5.2.3", {"start": v(59.5, 27.8) * mm, "end": v(59.5, 35.8) * mm});
            skLineSegment(sketch, "E8.5.3.0", {"start": v(59.5, 38.7) * mm, "end": v(67.5, 38.7) * mm});
            skLineSegment(sketch, "E8.5.3.1", {"start": v(67.5, 38.7) * mm, "end": v(67.5, 46.7) * mm});
            skLineSegment(sketch, "E8.5.3.2", {"start": v(59.5, 46.7) * mm, "end": v(67.5, 46.7) * mm});
            skLineSegment(sketch, "E8.5.3.3", {"start": v(59.5, 38.7) * mm, "end": v(59.5, 46.7) * mm});
            skLineSegment(sketch, "E8.5.4.0", {"start": v(59.5, 49.6) * mm, "end": v(67.5, 49.6) * mm});
            skLineSegment(sketch, "E8.5.4.1", {"start": v(67.5, 49.6) * mm, "end": v(67.5, 57.6) * mm});
            skLineSegment(sketch, "E8.5.4.2", {"start": v(59.5, 57.6) * mm, "end": v(67.5, 57.6) * mm});
            skLineSegment(sketch, "E8.5.4.3", {"start": v(59.5, 49.6) * mm, "end": v(59.5, 57.6) * mm});
            skLineSegment(sketch, "E8.5.5.0", {"start": v(59.5, 60.5) * mm, "end": v(67.5, 60.5) * mm});
            skLineSegment(sketch, "E8.5.5.1", {"start": v(67.5, 60.5) * mm, "end": v(67.5, 68.5) * mm});
            skLineSegment(sketch, "E8.5.5.2", {"start": v(59.5, 68.5) * mm, "end": v(67.5, 68.5) * mm});
            skLineSegment(sketch, "E8.5.5.3", {"start": v(59.5, 60.5) * mm, "end": v(59.5, 68.5) * mm});
            skLineSegment(sketch, "E8.5.6.0", {"start": v(59.5, 71.4) * mm, "end": v(67.5, 71.4) * mm});
            skLineSegment(sketch, "E8.5.6.1", {"start": v(67.5, 71.4) * mm, "end": v(67.5, 79.4) * mm});
            skLineSegment(sketch, "E8.5.6.2", {"start": v(59.5, 79.4) * mm, "end": v(67.5, 79.4) * mm});
            skLineSegment(sketch, "E8.5.6.3", {"start": v(59.5, 71.4) * mm, "end": v(59.5, 79.4) * mm});
            skLineSegment(sketch, "E8.5.7.0", {"start": v(59.5, 82.3) * mm, "end": v(67.5, 82.3) * mm});
            skLineSegment(sketch, "E8.5.7.1", {"start": v(67.5, 82.3) * mm, "end": v(67.5, 90.3) * mm});
            skLineSegment(sketch, "E8.5.7.2", {"start": v(59.5, 90.3) * mm, "end": v(67.5, 90.3) * mm});
            skLineSegment(sketch, "E8.5.7.3", {"start": v(59.5, 82.3) * mm, "end": v(59.5, 90.3) * mm});
            skLineSegment(sketch, "E8.5.8.0", {"start": v(59.5, 93.2) * mm, "end": v(67.5, 93.2) * mm});
            skLineSegment(sketch, "E8.5.8.1", {"start": v(67.5, 93.2) * mm, "end": v(67.5, 101.2) * mm});
            skLineSegment(sketch, "E8.5.8.2", {"start": v(59.5, 101.2) * mm, "end": v(67.5, 101.2) * mm});
            skLineSegment(sketch, "E8.5.8.3", {"start": v(59.5, 93.2) * mm, "end": v(59.5, 101.2) * mm});
            skLineSegment(sketch, "E8.5.9.0", {"start": v(59.5, 104.1) * mm, "end": v(67.5, 104.1) * mm});
            skLineSegment(sketch, "E8.5.9.1", {"start": v(67.5, 104.1) * mm, "end": v(67.5, 112.1) * mm});
            skLineSegment(sketch, "E8.5.9.2", {"start": v(59.5, 112.1) * mm, "end": v(67.5, 112.1) * mm});
            skLineSegment(sketch, "E8.5.9.3", {"start": v(59.5, 104.1) * mm, "end": v(59.5, 112.1) * mm});
            skLineSegment(sketch, "E8.5.10.0", {"start": v(59.5, 115) * mm, "end": v(67.5, 115) * mm});
            skLineSegment(sketch, "E8.5.10.1", {"start": v(67.5, 115) * mm, "end": v(67.5, 123) * mm});
            skLineSegment(sketch, "E8.5.10.2", {"start": v(59.5, 123) * mm, "end": v(67.5, 123) * mm});
            skLineSegment(sketch, "E8.5.10.3", {"start": v(59.5, 115) * mm, "end": v(59.5, 123) * mm});
            skLineSegment(sketch, "E8.5.11.0", {"start": v(59.5, 125.9) * mm, "end": v(67.5, 125.9) * mm});
            skLineSegment(sketch, "E8.5.11.1", {"start": v(67.5, 125.9) * mm, "end": v(67.5, 133.9) * mm});
            skLineSegment(sketch, "E8.5.11.2", {"start": v(59.5, 133.9) * mm, "end": v(67.5, 133.9) * mm});
            skLineSegment(sketch, "E8.5.11.3", {"start": v(59.5, 125.9) * mm, "end": v(59.5, 133.9) * mm});
            skLineSegment(sketch, "E8.6.0.0", {"start": v(70.2, 6) * mm, "end": v(78.2, 6) * mm});
            skLineSegment(sketch, "E8.6.0.1", {"start": v(78.2, 6) * mm, "end": v(78.2, 14) * mm});
            skLineSegment(sketch, "E8.6.0.2", {"start": v(70.2, 14) * mm, "end": v(78.2, 14) * mm});
            skLineSegment(sketch, "E8.6.0.3", {"start": v(70.2, 6) * mm, "end": v(70.2, 14) * mm});
            skLineSegment(sketch, "E8.6.1.0", {"start": v(70.2, 16.9) * mm, "end": v(78.2, 16.9) * mm});
            skLineSegment(sketch, "E8.6.1.1", {"start": v(78.2, 16.9) * mm, "end": v(78.2, 24.9) * mm});
            skLineSegment(sketch, "E8.6.1.2", {"start": v(70.2, 24.9) * mm, "end": v(78.2, 24.9) * mm});
            skLineSegment(sketch, "E8.6.1.3", {"start": v(70.2, 16.9) * mm, "end": v(70.2, 24.9) * mm});
            skLineSegment(sketch, "E8.6.2.0", {"start": v(70.2, 27.8) * mm, "end": v(78.2, 27.8) * mm});
            skLineSegment(sketch, "E8.6.2.1", {"start": v(78.2, 27.8) * mm, "end": v(78.2, 35.8) * mm});
            skLineSegment(sketch, "E8.6.2.2", {"start": v(70.2, 35.8) * mm, "end": v(78.2, 35.8) * mm});
            skLineSegment(sketch, "E8.6.2.3", {"start": v(70.2, 27.8) * mm, "end": v(70.2, 35.8) * mm});
            skLineSegment(sketch, "E8.6.3.0", {"start": v(70.2, 38.7) * mm, "end": v(78.2, 38.7) * mm});
            skLineSegment(sketch, "E8.6.3.1", {"start": v(78.2, 38.7) * mm, "end": v(78.2, 46.7) * mm});
            skLineSegment(sketch, "E8.6.3.2", {"start": v(70.2, 46.7) * mm, "end": v(78.2, 46.7) * mm});
            skLineSegment(sketch, "E8.6.3.3", {"start": v(70.2, 38.7) * mm, "end": v(70.2, 46.7) * mm});
            skLineSegment(sketch, "E8.6.4.0", {"start": v(70.2, 49.6) * mm, "end": v(78.2, 49.6) * mm});
            skLineSegment(sketch, "E8.6.4.1", {"start": v(78.2, 49.6) * mm, "end": v(78.2, 57.6) * mm});
            skLineSegment(sketch, "E8.6.4.2", {"start": v(70.2, 57.6) * mm, "end": v(78.2, 57.6) * mm});
            skLineSegment(sketch, "E8.6.4.3", {"start": v(70.2, 49.6) * mm, "end": v(70.2, 57.6) * mm});
            skLineSegment(sketch, "E8.6.5.0", {"start": v(70.2, 60.5) * mm, "end": v(78.2, 60.5) * mm});
            skLineSegment(sketch, "E8.6.5.1", {"start": v(78.2, 60.5) * mm, "end": v(78.2, 68.5) * mm});
            skLineSegment(sketch, "E8.6.5.2", {"start": v(70.2, 68.5) * mm, "end": v(78.2, 68.5) * mm});
            skLineSegment(sketch, "E8.6.5.3", {"start": v(70.2, 60.5) * mm, "end": v(70.2, 68.5) * mm});
            skLineSegment(sketch, "E8.6.6.0", {"start": v(70.2, 71.4) * mm, "end": v(78.2, 71.4) * mm});
            skLineSegment(sketch, "E8.6.6.1", {"start": v(78.2, 71.4) * mm, "end": v(78.2, 79.4) * mm});
            skLineSegment(sketch, "E8.6.6.2", {"start": v(70.2, 79.4) * mm, "end": v(78.2, 79.4) * mm});
            skLineSegment(sketch, "E8.6.6.3", {"start": v(70.2, 71.4) * mm, "end": v(70.2, 79.4) * mm});
            skLineSegment(sketch, "E8.6.7.0", {"start": v(70.2, 82.3) * mm, "end": v(78.2, 82.3) * mm});
            skLineSegment(sketch, "E8.6.7.1", {"start": v(78.2, 82.3) * mm, "end": v(78.2, 90.3) * mm});
            skLineSegment(sketch, "E8.6.7.2", {"start": v(70.2, 90.3) * mm, "end": v(78.2, 90.3) * mm});
            skLineSegment(sketch, "E8.6.7.3", {"start": v(70.2, 82.3) * mm, "end": v(70.2, 90.3) * mm});
            skLineSegment(sketch, "E8.6.8.0", {"start": v(70.2, 93.2) * mm, "end": v(78.2, 93.2) * mm});
            skLineSegment(sketch, "E8.6.8.1", {"start": v(78.2, 93.2) * mm, "end": v(78.2, 101.2) * mm});
            skLineSegment(sketch, "E8.6.8.2", {"start": v(70.2, 101.2) * mm, "end": v(78.2, 101.2) * mm});
            skLineSegment(sketch, "E8.6.8.3", {"start": v(70.2, 93.2) * mm, "end": v(70.2, 101.2) * mm});
            skLineSegment(sketch, "E8.6.9.0", {"start": v(70.2, 104.1) * mm, "end": v(78.2, 104.1) * mm});
            skLineSegment(sketch, "E8.6.9.1", {"start": v(78.2, 104.1) * mm, "end": v(78.2, 112.1) * mm});
            skLineSegment(sketch, "E8.6.9.2", {"start": v(70.2, 112.1) * mm, "end": v(78.2, 112.1) * mm});
            skLineSegment(sketch, "E8.6.9.3", {"start": v(70.2, 104.1) * mm, "end": v(70.2, 112.1) * mm});
            skLineSegment(sketch, "E8.6.10.0", {"start": v(70.2, 115) * mm, "end": v(78.2, 115) * mm});
            skLineSegment(sketch, "E8.6.10.1", {"start": v(78.2, 115) * mm, "end": v(78.2, 123) * mm});
            skLineSegment(sketch, "E8.6.10.2", {"start": v(70.2, 123) * mm, "end": v(78.2, 123) * mm});
            skLineSegment(sketch, "E8.6.10.3", {"start": v(70.2, 115) * mm, "end": v(70.2, 123) * mm});
            skLineSegment(sketch, "E8.6.11.0", {"start": v(70.2, 125.9) * mm, "end": v(78.2, 125.9) * mm});
            skLineSegment(sketch, "E8.6.11.1", {"start": v(78.2, 125.9) * mm, "end": v(78.2, 133.9) * mm});
            skLineSegment(sketch, "E8.6.11.2", {"start": v(70.2, 133.9) * mm, "end": v(78.2, 133.9) * mm});
            skLineSegment(sketch, "E8.6.11.3", {"start": v(70.2, 125.9) * mm, "end": v(70.2, 133.9) * mm});
            skLineSegment(sketch, "E8.7.0.0", {"start": v(80.9, 6) * mm, "end": v(88.9, 6) * mm});
            skLineSegment(sketch, "E8.7.0.1", {"start": v(88.9, 6) * mm, "end": v(88.9, 14) * mm});
            skLineSegment(sketch, "E8.7.0.2", {"start": v(80.9, 14) * mm, "end": v(88.9, 14) * mm});
            skLineSegment(sketch, "E8.7.0.3", {"start": v(80.9, 6) * mm, "end": v(80.9, 14) * mm});
            skLineSegment(sketch, "E8.7.1.0", {"start": v(80.9, 16.9) * mm, "end": v(88.9, 16.9) * mm});
            skLineSegment(sketch, "E8.7.1.1", {"start": v(88.9, 16.9) * mm, "end": v(88.9, 24.9) * mm});
            skLineSegment(sketch, "E8.7.1.2", {"start": v(80.9, 24.9) * mm, "end": v(88.9, 24.9) * mm});
            skLineSegment(sketch, "E8.7.1.3", {"start": v(80.9, 16.9) * mm, "end": v(80.9, 24.9) * mm});
            skLineSegment(sketch, "E8.7.2.0", {"start": v(80.9, 27.8) * mm, "end": v(88.9, 27.8) * mm});
            skLineSegment(sketch, "E8.7.2.1", {"start": v(88.9, 27.8) * mm, "end": v(88.9, 35.8) * mm});
            skLineSegment(sketch, "E8.7.2.2", {"start": v(80.9, 35.8) * mm, "end": v(88.9, 35.8) * mm});
            skLineSegment(sketch, "E8.7.2.3", {"start": v(80.9, 27.8) * mm, "end": v(80.9, 35.8) * mm});
            skLineSegment(sketch, "E8.7.3.0", {"start": v(80.9, 38.7) * mm, "end": v(88.9, 38.7) * mm});
            skLineSegment(sketch, "E8.7.3.1", {"start": v(88.9, 38.7) * mm, "end": v(88.9, 46.7) * mm});
            skLineSegment(sketch, "E8.7.3.2", {"start": v(80.9, 46.7) * mm, "end": v(88.9, 46.7) * mm});
            skLineSegment(sketch, "E8.7.3.3", {"start": v(80.9, 38.7) * mm, "end": v(80.9, 46.7) * mm});
            skLineSegment(sketch, "E8.7.4.0", {"start": v(80.9, 49.6) * mm, "end": v(88.9, 49.6) * mm});
            skLineSegment(sketch, "E8.7.4.1", {"start": v(88.9, 49.6) * mm, "end": v(88.9, 57.6) * mm});
            skLineSegment(sketch, "E8.7.4.2", {"start": v(80.9, 57.6) * mm, "end": v(88.9, 57.6) * mm});
            skLineSegment(sketch, "E8.7.4.3", {"start": v(80.9, 49.6) * mm, "end": v(80.9, 57.6) * mm});
            skLineSegment(sketch, "E8.7.5.0", {"start": v(80.9, 60.5) * mm, "end": v(88.9, 60.5) * mm});
            skLineSegment(sketch, "E8.7.5.1", {"start": v(88.9, 60.5) * mm, "end": v(88.9, 68.5) * mm});
            skLineSegment(sketch, "E8.7.5.2", {"start": v(80.9, 68.5) * mm, "end": v(88.9, 68.5) * mm});
            skLineSegment(sketch, "E8.7.5.3", {"start": v(80.9, 60.5) * mm, "end": v(80.9, 68.5) * mm});
            skLineSegment(sketch, "E8.7.6.0", {"start": v(80.9, 71.4) * mm, "end": v(88.9, 71.4) * mm});
            skLineSegment(sketch, "E8.7.6.1", {"start": v(88.9, 71.4) * mm, "end": v(88.9, 79.4) * mm});
            skLineSegment(sketch, "E8.7.6.2", {"start": v(80.9, 79.4) * mm, "end": v(88.9, 79.4) * mm});
            skLineSegment(sketch, "E8.7.6.3", {"start": v(80.9, 71.4) * mm, "end": v(80.9, 79.4) * mm});
            skLineSegment(sketch, "E8.7.7.0", {"start": v(80.9, 82.3) * mm, "end": v(88.9, 82.3) * mm});
            skLineSegment(sketch, "E8.7.7.1", {"start": v(88.9, 82.3) * mm, "end": v(88.9, 90.3) * mm});
            skLineSegment(sketch, "E8.7.7.2", {"start": v(80.9, 90.3) * mm, "end": v(88.9, 90.3) * mm});
            skLineSegment(sketch, "E8.7.7.3", {"start": v(80.9, 82.3) * mm, "end": v(80.9, 90.3) * mm});
            skLineSegment(sketch, "E8.7.8.0", {"start": v(80.9, 93.2) * mm, "end": v(88.9, 93.2) * mm});
            skLineSegment(sketch, "E8.7.8.1", {"start": v(88.9, 93.2) * mm, "end": v(88.9, 101.2) * mm});
            skLineSegment(sketch, "E8.7.8.2", {"start": v(80.9, 101.2) * mm, "end": v(88.9, 101.2) * mm});
            skLineSegment(sketch, "E8.7.8.3", {"start": v(80.9, 93.2) * mm, "end": v(80.9, 101.2) * mm});
            skLineSegment(sketch, "E8.7.9.0", {"start": v(80.9, 104.1) * mm, "end": v(88.9, 104.1) * mm});
            skLineSegment(sketch, "E8.7.9.1", {"start": v(88.9, 104.1) * mm, "end": v(88.9, 112.1) * mm});
            skLineSegment(sketch, "E8.7.9.2", {"start": v(80.9, 112.1) * mm, "end": v(88.9, 112.1) * mm});
            skLineSegment(sketch, "E8.7.9.3", {"start": v(80.9, 104.1) * mm, "end": v(80.9, 112.1) * mm});
            skLineSegment(sketch, "E8.7.10.0", {"start": v(80.9, 115) * mm, "end": v(88.9, 115) * mm});
            skLineSegment(sketch, "E8.7.10.1", {"start": v(88.9, 115) * mm, "end": v(88.9, 123) * mm});
            skLineSegment(sketch, "E8.7.10.2", {"start": v(80.9, 123) * mm, "end": v(88.9, 123) * mm});
            skLineSegment(sketch, "E8.7.10.3", {"start": v(80.9, 115) * mm, "end": v(80.9, 123) * mm});
            skLineSegment(sketch, "E8.7.11.0", {"start": v(80.9, 125.9) * mm, "end": v(88.9, 125.9) * mm});
            skLineSegment(sketch, "E8.7.11.1", {"start": v(88.9, 125.9) * mm, "end": v(88.9, 133.9) * mm});
            skLineSegment(sketch, "E8.7.11.2", {"start": v(80.9, 133.9) * mm, "end": v(88.9, 133.9) * mm});
            skLineSegment(sketch, "E8.7.11.3", {"start": v(80.9, 125.9) * mm, "end": v(80.9, 133.9) * mm});
            skLineSegment(sketch, "E8.8.0.0", {"start": v(91.6, 6) * mm, "end": v(99.6, 6) * mm});
            skLineSegment(sketch, "E8.8.0.1", {"start": v(99.6, 6) * mm, "end": v(99.6, 14) * mm});
            skLineSegment(sketch, "E8.8.0.2", {"start": v(91.6, 14) * mm, "end": v(99.6, 14) * mm});
            skLineSegment(sketch, "E8.8.0.3", {"start": v(91.6, 6) * mm, "end": v(91.6, 14) * mm});
            skLineSegment(sketch, "E8.8.1.0", {"start": v(91.6, 16.9) * mm, "end": v(99.6, 16.9) * mm});
            skLineSegment(sketch, "E8.8.1.1", {"start": v(99.6, 16.9) * mm, "end": v(99.6, 24.9) * mm});
            skLineSegment(sketch, "E8.8.1.2", {"start": v(91.6, 24.9) * mm, "end": v(99.6, 24.9) * mm});
            skLineSegment(sketch, "E8.8.1.3", {"start": v(91.6, 16.9) * mm, "end": v(91.6, 24.9) * mm});
            skLineSegment(sketch, "E8.8.2.0", {"start": v(91.6, 27.8) * mm, "end": v(99.6, 27.8) * mm});
            skLineSegment(sketch, "E8.8.2.1", {"start": v(99.6, 27.8) * mm, "end": v(99.6, 35.8) * mm});
            skLineSegment(sketch, "E8.8.2.2", {"start": v(91.6, 35.8) * mm, "end": v(99.6, 35.8) * mm});
            skLineSegment(sketch, "E8.8.2.3", {"start": v(91.6, 27.8) * mm, "end": v(91.6, 35.8) * mm});
            skLineSegment(sketch, "E8.8.3.0", {"start": v(91.6, 38.7) * mm, "end": v(99.6, 38.7) * mm});
            skLineSegment(sketch, "E8.8.3.1", {"start": v(99.6, 38.7) * mm, "end": v(99.6, 46.7) * mm});
            skLineSegment(sketch, "E8.8.3.2", {"start": v(91.6, 46.7) * mm, "end": v(99.6, 46.7) * mm});
            skLineSegment(sketch, "E8.8.3.3", {"start": v(91.6, 38.7) * mm, "end": v(91.6, 46.7) * mm});
            skLineSegment(sketch, "E8.8.4.0", {"start": v(91.6, 49.6) * mm, "end": v(99.6, 49.6) * mm});
            skLineSegment(sketch, "E8.8.4.1", {"start": v(99.6, 49.6) * mm, "end": v(99.6, 57.6) * mm});
            skLineSegment(sketch, "E8.8.4.2", {"start": v(91.6, 57.6) * mm, "end": v(99.6, 57.6) * mm});
            skLineSegment(sketch, "E8.8.4.3", {"start": v(91.6, 49.6) * mm, "end": v(91.6, 57.6) * mm});
            skLineSegment(sketch, "E8.8.5.0", {"start": v(91.6, 60.5) * mm, "end": v(99.6, 60.5) * mm});
            skLineSegment(sketch, "E8.8.5.1", {"start": v(99.6, 60.5) * mm, "end": v(99.6, 68.5) * mm});
            skLineSegment(sketch, "E8.8.5.2", {"start": v(91.6, 68.5) * mm, "end": v(99.6, 68.5) * mm});
            skLineSegment(sketch, "E8.8.5.3", {"start": v(91.6, 60.5) * mm, "end": v(91.6, 68.5) * mm});
            skLineSegment(sketch, "E8.8.6.0", {"start": v(91.6, 71.4) * mm, "end": v(99.6, 71.4) * mm});
            skLineSegment(sketch, "E8.8.6.1", {"start": v(99.6, 71.4) * mm, "end": v(99.6, 79.4) * mm});
            skLineSegment(sketch, "E8.8.6.2", {"start": v(91.6, 79.4) * mm, "end": v(99.6, 79.4) * mm});
            skLineSegment(sketch, "E8.8.6.3", {"start": v(91.6, 71.4) * mm, "end": v(91.6, 79.4) * mm});
            skLineSegment(sketch, "E8.8.7.0", {"start": v(91.6, 82.3) * mm, "end": v(99.6, 82.3) * mm});
            skLineSegment(sketch, "E8.8.7.1", {"start": v(99.6, 82.3) * mm, "end": v(99.6, 90.3) * mm});
            skLineSegment(sketch, "E8.8.7.2", {"start": v(91.6, 90.3) * mm, "end": v(99.6, 90.3) * mm});
            skLineSegment(sketch, "E8.8.7.3", {"start": v(91.6, 82.3) * mm, "end": v(91.6, 90.3) * mm});
            skLineSegment(sketch, "E8.8.8.0", {"start": v(91.6, 93.2) * mm, "end": v(99.6, 93.2) * mm});
            skLineSegment(sketch, "E8.8.8.1", {"start": v(99.6, 93.2) * mm, "end": v(99.6, 101.2) * mm});
            skLineSegment(sketch, "E8.8.8.2", {"start": v(91.6, 101.2) * mm, "end": v(99.6, 101.2) * mm});
            skLineSegment(sketch, "E8.8.8.3", {"start": v(91.6, 93.2) * mm, "end": v(91.6, 101.2) * mm});
            skLineSegment(sketch, "E8.8.9.0", {"start": v(91.6, 104.1) * mm, "end": v(99.6, 104.1) * mm});
            skLineSegment(sketch, "E8.8.9.1", {"start": v(99.6, 104.1) * mm, "end": v(99.6, 112.1) * mm});
            skLineSegment(sketch, "E8.8.9.2", {"start": v(91.6, 112.1) * mm, "end": v(99.6, 112.1) * mm});
            skLineSegment(sketch, "E8.8.9.3", {"start": v(91.6, 104.1) * mm, "end": v(91.6, 112.1) * mm});
            skLineSegment(sketch, "E8.8.10.0", {"start": v(91.6, 115) * mm, "end": v(99.6, 115) * mm});
            skLineSegment(sketch, "E8.8.10.1", {"start": v(99.6, 115) * mm, "end": v(99.6, 123) * mm});
            skLineSegment(sketch, "E8.8.10.2", {"start": v(91.6, 123) * mm, "end": v(99.6, 123) * mm});
            skLineSegment(sketch, "E8.8.10.3", {"start": v(91.6, 115) * mm, "end": v(91.6, 123) * mm});
            skLineSegment(sketch, "E8.8.11.0", {"start": v(91.6, 125.9) * mm, "end": v(99.6, 125.9) * mm});
            skLineSegment(sketch, "E8.8.11.1", {"start": v(99.6, 125.9) * mm, "end": v(99.6, 133.9) * mm});
            skLineSegment(sketch, "E8.8.11.2", {"start": v(91.6, 133.9) * mm, "end": v(99.6, 133.9) * mm});
            skLineSegment(sketch, "E8.8.11.3", {"start": v(91.6, 125.9) * mm, "end": v(91.6, 133.9) * mm});
            skLineSegment(sketch, "E8.9.0.0", {"start": v(102.3, 6) * mm, "end": v(110.3, 6) * mm});
            skLineSegment(sketch, "E8.9.0.1", {"start": v(110.3, 6) * mm, "end": v(110.3, 14) * mm});
            skLineSegment(sketch, "E8.9.0.2", {"start": v(102.3, 14) * mm, "end": v(110.3, 14) * mm});
            skLineSegment(sketch, "E8.9.0.3", {"start": v(102.3, 6) * mm, "end": v(102.3, 14) * mm});
            skLineSegment(sketch, "E8.9.1.0", {"start": v(102.3, 16.9) * mm, "end": v(110.3, 16.9) * mm});
            skLineSegment(sketch, "E8.9.1.1", {"start": v(110.3, 16.9) * mm, "end": v(110.3, 24.9) * mm});
            skLineSegment(sketch, "E8.9.1.2", {"start": v(102.3, 24.9) * mm, "end": v(110.3, 24.9) * mm});
            skLineSegment(sketch, "E8.9.1.3", {"start": v(102.3, 16.9) * mm, "end": v(102.3, 24.9) * mm});
            skLineSegment(sketch, "E8.9.2.0", {"start": v(102.3, 27.8) * mm, "end": v(110.3, 27.8) * mm});
            skLineSegment(sketch, "E8.9.2.1", {"start": v(110.3, 27.8) * mm, "end": v(110.3, 35.8) * mm});
            skLineSegment(sketch, "E8.9.2.2", {"start": v(102.3, 35.8) * mm, "end": v(110.3, 35.8) * mm});
            skLineSegment(sketch, "E8.9.2.3", {"start": v(102.3, 27.8) * mm, "end": v(102.3, 35.8) * mm});
            skLineSegment(sketch, "E8.9.3.0", {"start": v(102.3, 38.7) * mm, "end": v(110.3, 38.7) * mm});
            skLineSegment(sketch, "E8.9.3.1", {"start": v(110.3, 38.7) * mm, "end": v(110.3, 46.7) * mm});
            skLineSegment(sketch, "E8.9.3.2", {"start": v(102.3, 46.7) * mm, "end": v(110.3, 46.7) * mm});
            skLineSegment(sketch, "E8.9.3.3", {"start": v(102.3, 38.7) * mm, "end": v(102.3, 46.7) * mm});
            skLineSegment(sketch, "E8.9.4.0", {"start": v(102.3, 49.6) * mm, "end": v(110.3, 49.6) * mm});
            skLineSegment(sketch, "E8.9.4.1", {"start": v(110.3, 49.6) * mm, "end": v(110.3, 57.6) * mm});
            skLineSegment(sketch, "E8.9.4.2", {"start": v(102.3, 57.6) * mm, "end": v(110.3, 57.6) * mm});
            skLineSegment(sketch, "E8.9.4.3", {"start": v(102.3, 49.6) * mm, "end": v(102.3, 57.6) * mm});
            skLineSegment(sketch, "E8.9.5.0", {"start": v(102.3, 60.5) * mm, "end": v(110.3, 60.5) * mm});
            skLineSegment(sketch, "E8.9.5.1", {"start": v(110.3, 60.5) * mm, "end": v(110.3, 68.5) * mm});
            skLineSegment(sketch, "E8.9.5.2", {"start": v(102.3, 68.5) * mm, "end": v(110.3, 68.5) * mm});
            skLineSegment(sketch, "E8.9.5.3", {"start": v(102.3, 60.5) * mm, "end": v(102.3, 68.5) * mm});
            skLineSegment(sketch, "E8.9.6.0", {"start": v(102.3, 71.4) * mm, "end": v(110.3, 71.4) * mm});
            skLineSegment(sketch, "E8.9.6.1", {"start": v(110.3, 71.4) * mm, "end": v(110.3, 79.4) * mm});
            skLineSegment(sketch, "E8.9.6.2", {"start": v(102.3, 79.4) * mm, "end": v(110.3, 79.4) * mm});
            skLineSegment(sketch, "E8.9.6.3", {"start": v(102.3, 71.4) * mm, "end": v(102.3, 79.4) * mm});
            skLineSegment(sketch, "E8.9.7.0", {"start": v(102.3, 82.3) * mm, "end": v(110.3, 82.3) * mm});
            skLineSegment(sketch, "E8.9.7.1", {"start": v(110.3, 82.3) * mm, "end": v(110.3, 90.3) * mm});
            skLineSegment(sketch, "E8.9.7.2", {"start": v(102.3, 90.3) * mm, "end": v(110.3, 90.3) * mm});
            skLineSegment(sketch, "E8.9.7.3", {"start": v(102.3, 82.3) * mm, "end": v(102.3, 90.3) * mm});
            skLineSegment(sketch, "E8.9.8.0", {"start": v(102.3, 93.2) * mm, "end": v(110.3, 93.2) * mm});
            skLineSegment(sketch, "E8.9.8.1", {"start": v(110.3, 93.2) * mm, "end": v(110.3, 101.2) * mm});
            skLineSegment(sketch, "E8.9.8.2", {"start": v(102.3, 101.2) * mm, "end": v(110.3, 101.2) * mm});
            skLineSegment(sketch, "E8.9.8.3", {"start": v(102.3, 93.2) * mm, "end": v(102.3, 101.2) * mm});
            skLineSegment(sketch, "E8.9.9.0", {"start": v(102.3, 104.1) * mm, "end": v(110.3, 104.1) * mm});
            skLineSegment(sketch, "E8.9.9.1", {"start": v(110.3, 104.1) * mm, "end": v(110.3, 112.1) * mm});
            skLineSegment(sketch, "E8.9.9.2", {"start": v(102.3, 112.1) * mm, "end": v(110.3, 112.1) * mm});
            skLineSegment(sketch, "E8.9.9.3", {"start": v(102.3, 104.1) * mm, "end": v(102.3, 112.1) * mm});
            skLineSegment(sketch, "E8.9.10.0", {"start": v(102.3, 115) * mm, "end": v(110.3, 115) * mm});
            skLineSegment(sketch, "E8.9.10.1", {"start": v(110.3, 115) * mm, "end": v(110.3, 123) * mm});
            skLineSegment(sketch, "E8.9.10.2", {"start": v(102.3, 123) * mm, "end": v(110.3, 123) * mm});
            skLineSegment(sketch, "E8.9.10.3", {"start": v(102.3, 115) * mm, "end": v(102.3, 123) * mm});
            skLineSegment(sketch, "E8.9.11.0", {"start": v(102.3, 125.9) * mm, "end": v(110.3, 125.9) * mm});
            skLineSegment(sketch, "E8.9.11.1", {"start": v(110.3, 125.9) * mm, "end": v(110.3, 133.9) * mm});
            skLineSegment(sketch, "E8.9.11.2", {"start": v(102.3, 133.9) * mm, "end": v(110.3, 133.9) * mm});
            skLineSegment(sketch, "E8.9.11.3", {"start": v(102.3, 125.9) * mm, "end": v(102.3, 133.9) * mm});
            skLineSegment(sketch, "E8.10.0.0", {"start": v(113, 6) * mm, "end": v(121, 6) * mm});
            skLineSegment(sketch, "E8.10.0.1", {"start": v(121, 6) * mm, "end": v(121, 14) * mm});
            skLineSegment(sketch, "E8.10.0.2", {"start": v(113, 14) * mm, "end": v(121, 14) * mm});
            skLineSegment(sketch, "E8.10.0.3", {"start": v(113, 6) * mm, "end": v(113, 14) * mm});
            skLineSegment(sketch, "E8.10.1.0", {"start": v(113, 16.9) * mm, "end": v(121, 16.9) * mm});
            skLineSegment(sketch, "E8.10.1.1", {"start": v(121, 16.9) * mm, "end": v(121, 24.9) * mm});
            skLineSegment(sketch, "E8.10.1.2", {"start": v(113, 24.9) * mm, "end": v(121, 24.9) * mm});
            skLineSegment(sketch, "E8.10.1.3", {"start": v(113, 16.9) * mm, "end": v(113, 24.9) * mm});
            skLineSegment(sketch, "E8.10.2.0", {"start": v(113, 27.8) * mm, "end": v(121, 27.8) * mm});
            skLineSegment(sketch, "E8.10.2.1", {"start": v(121, 27.8) * mm, "end": v(121, 35.8) * mm});
            skLineSegment(sketch, "E8.10.2.2", {"start": v(113, 35.8) * mm, "end": v(121, 35.8) * mm});
            skLineSegment(sketch, "E8.10.2.3", {"start": v(113, 27.8) * mm, "end": v(113, 35.8) * mm});
            skLineSegment(sketch, "E8.10.3.0", {"start": v(113, 38.7) * mm, "end": v(121, 38.7) * mm});
            skLineSegment(sketch, "E8.10.3.1", {"start": v(121, 38.7) * mm, "end": v(121, 46.7) * mm});
            skLineSegment(sketch, "E8.10.3.2", {"start": v(113, 46.7) * mm, "end": v(121, 46.7) * mm});
            skLineSegment(sketch, "E8.10.3.3", {"start": v(113, 38.7) * mm, "end": v(113, 46.7) * mm});
            skLineSegment(sketch, "E8.10.4.0", {"start": v(113, 49.6) * mm, "end": v(121, 49.6) * mm});
            skLineSegment(sketch, "E8.10.4.1", {"start": v(121, 49.6) * mm, "end": v(121, 57.6) * mm});
            skLineSegment(sketch, "E8.10.4.2", {"start": v(113, 57.6) * mm, "end": v(121, 57.6) * mm});
            skLineSegment(sketch, "E8.10.4.3", {"start": v(113, 49.6) * mm, "end": v(113, 57.6) * mm});
            skLineSegment(sketch, "E8.10.5.0", {"start": v(113, 60.5) * mm, "end": v(121, 60.5) * mm});
            skLineSegment(sketch, "E8.10.5.1", {"start": v(121, 60.5) * mm, "end": v(121, 68.5) * mm});
            skLineSegment(sketch, "E8.10.5.2", {"start": v(113, 68.5) * mm, "end": v(121, 68.5) * mm});
            skLineSegment(sketch, "E8.10.5.3", {"start": v(113, 60.5) * mm, "end": v(113, 68.5) * mm});
            skLineSegment(sketch, "E8.10.6.0", {"start": v(113, 71.4) * mm, "end": v(121, 71.4) * mm});
            skLineSegment(sketch, "E8.10.6.1", {"start": v(121, 71.4) * mm, "end": v(121, 79.4) * mm});
            skLineSegment(sketch, "E8.10.6.2", {"start": v(113, 79.4) * mm, "end": v(121, 79.4) * mm});
            skLineSegment(sketch, "E8.10.6.3", {"start": v(113, 71.4) * mm, "end": v(113, 79.4) * mm});
            skLineSegment(sketch, "E8.10.7.0", {"start": v(113, 82.3) * mm, "end": v(121, 82.3) * mm});
            skLineSegment(sketch, "E8.10.7.1", {"start": v(121, 82.3) * mm, "end": v(121, 90.3) * mm});
            skLineSegment(sketch, "E8.10.7.2", {"start": v(113, 90.3) * mm, "end": v(121, 90.3) * mm});
            skLineSegment(sketch, "E8.10.7.3", {"start": v(113, 82.3) * mm, "end": v(113, 90.3) * mm});
            skLineSegment(sketch, "E8.10.8.0", {"start": v(113, 93.2) * mm, "end": v(121, 93.2) * mm});
            skLineSegment(sketch, "E8.10.8.1", {"start": v(121, 93.2) * mm, "end": v(121, 101.2) * mm});
            skLineSegment(sketch, "E8.10.8.2", {"start": v(113, 101.2) * mm, "end": v(121, 101.2) * mm});
            skLineSegment(sketch, "E8.10.8.3", {"start": v(113, 93.2) * mm, "end": v(113, 101.2) * mm});
            skLineSegment(sketch, "E8.10.9.0", {"start": v(113, 104.1) * mm, "end": v(121, 104.1) * mm});
            skLineSegment(sketch, "E8.10.9.1", {"start": v(121, 104.1) * mm, "end": v(121, 112.1) * mm});
            skLineSegment(sketch, "E8.10.9.2", {"start": v(113, 112.1) * mm, "end": v(121, 112.1) * mm});
            skLineSegment(sketch, "E8.10.9.3", {"start": v(113, 104.1) * mm, "end": v(113, 112.1) * mm});
            skLineSegment(sketch, "E8.10.10.0", {"start": v(113, 115) * mm, "end": v(121, 115) * mm});
            skLineSegment(sketch, "E8.10.10.1", {"start": v(121, 115) * mm, "end": v(121, 123) * mm});
            skLineSegment(sketch, "E8.10.10.2", {"start": v(113, 123) * mm, "end": v(121, 123) * mm});
            skLineSegment(sketch, "E8.10.10.3", {"start": v(113, 115) * mm, "end": v(113, 123) * mm});
            skLineSegment(sketch, "E8.10.11.0", {"start": v(113, 125.9) * mm, "end": v(121, 125.9) * mm});
            skLineSegment(sketch, "E8.10.11.1", {"start": v(121, 125.9) * mm, "end": v(121, 133.9) * mm});
            skLineSegment(sketch, "E8.10.11.2", {"start": v(113, 133.9) * mm, "end": v(121, 133.9) * mm});
            skLineSegment(sketch, "E8.10.11.3", {"start": v(113, 125.9) * mm, "end": v(113, 133.9) * mm});
            skLineSegment(sketch, "E8.11.0.0", {"start": v(123.7, 6) * mm, "end": v(131.7, 6) * mm});
            skLineSegment(sketch, "E8.11.0.1", {"start": v(131.7, 6) * mm, "end": v(131.7, 14) * mm});
            skLineSegment(sketch, "E8.11.0.2", {"start": v(123.7, 14) * mm, "end": v(131.7, 14) * mm});
            skLineSegment(sketch, "E8.11.0.3", {"start": v(123.7, 6) * mm, "end": v(123.7, 14) * mm});
            skLineSegment(sketch, "E8.11.1.0", {"start": v(123.7, 16.9) * mm, "end": v(131.7, 16.9) * mm});
            skLineSegment(sketch, "E8.11.1.1", {"start": v(131.7, 16.9) * mm, "end": v(131.7, 24.9) * mm});
            skLineSegment(sketch, "E8.11.1.2", {"start": v(123.7, 24.9) * mm, "end": v(131.7, 24.9) * mm});
            skLineSegment(sketch, "E8.11.1.3", {"start": v(123.7, 16.9) * mm, "end": v(123.7, 24.9) * mm});
            skLineSegment(sketch, "E8.11.2.0", {"start": v(123.7, 27.8) * mm, "end": v(131.7, 27.8) * mm});
            skLineSegment(sketch, "E8.11.2.1", {"start": v(131.7, 27.8) * mm, "end": v(131.7, 35.8) * mm});
            skLineSegment(sketch, "E8.11.2.2", {"start": v(123.7, 35.8) * mm, "end": v(131.7, 35.8) * mm});
            skLineSegment(sketch, "E8.11.2.3", {"start": v(123.7, 27.8) * mm, "end": v(123.7, 35.8) * mm});
            skLineSegment(sketch, "E8.11.3.0", {"start": v(123.7, 38.7) * mm, "end": v(131.7, 38.7) * mm});
            skLineSegment(sketch, "E8.11.3.1", {"start": v(131.7, 38.7) * mm, "end": v(131.7, 46.7) * mm});
            skLineSegment(sketch, "E8.11.3.2", {"start": v(123.7, 46.7) * mm, "end": v(131.7, 46.7) * mm});
            skLineSegment(sketch, "E8.11.3.3", {"start": v(123.7, 38.7) * mm, "end": v(123.7, 46.7) * mm});
            skLineSegment(sketch, "E8.11.4.0", {"start": v(123.7, 49.6) * mm, "end": v(131.7, 49.6) * mm});
            skLineSegment(sketch, "E8.11.4.1", {"start": v(131.7, 49.6) * mm, "end": v(131.7, 57.6) * mm});
            skLineSegment(sketch, "E8.11.4.2", {"start": v(123.7, 57.6) * mm, "end": v(131.7, 57.6) * mm});
            skLineSegment(sketch, "E8.11.4.3", {"start": v(123.7, 49.6) * mm, "end": v(123.7, 57.6) * mm});
            skLineSegment(sketch, "E8.11.5.0", {"start": v(123.7, 60.5) * mm, "end": v(131.7, 60.5) * mm});
            skLineSegment(sketch, "E8.11.5.1", {"start": v(131.7, 60.5) * mm, "end": v(131.7, 68.5) * mm});
            skLineSegment(sketch, "E8.11.5.2", {"start": v(123.7, 68.5) * mm, "end": v(131.7, 68.5) * mm});
            skLineSegment(sketch, "E8.11.5.3", {"start": v(123.7, 60.5) * mm, "end": v(123.7, 68.5) * mm});
            skLineSegment(sketch, "E8.11.6.0", {"start": v(123.7, 71.4) * mm, "end": v(131.7, 71.4) * mm});
            skLineSegment(sketch, "E8.11.6.1", {"start": v(131.7, 71.4) * mm, "end": v(131.7, 79.4) * mm});
            skLineSegment(sketch, "E8.11.6.2", {"start": v(123.7, 79.4) * mm, "end": v(131.7, 79.4) * mm});
            skLineSegment(sketch, "E8.11.6.3", {"start": v(123.7, 71.4) * mm, "end": v(123.7, 79.4) * mm});
            skLineSegment(sketch, "E8.11.7.0", {"start": v(123.7, 82.3) * mm, "end": v(131.7, 82.3) * mm});
            skLineSegment(sketch, "E8.11.7.1", {"start": v(131.7, 82.3) * mm, "end": v(131.7, 90.3) * mm});
            skLineSegment(sketch, "E8.11.7.2", {"start": v(123.7, 90.3) * mm, "end": v(131.7, 90.3) * mm});
            skLineSegment(sketch, "E8.11.7.3", {"start": v(123.7, 82.3) * mm, "end": v(123.7, 90.3) * mm});
            skLineSegment(sketch, "E8.11.8.0", {"start": v(123.7, 93.2) * mm, "end": v(131.7, 93.2) * mm});
            skLineSegment(sketch, "E8.11.8.1", {"start": v(131.7, 93.2) * mm, "end": v(131.7, 101.2) * mm});
            skLineSegment(sketch, "E8.11.8.2", {"start": v(123.7, 101.2) * mm, "end": v(131.7, 101.2) * mm});
            skLineSegment(sketch, "E8.11.8.3", {"start": v(123.7, 93.2) * mm, "end": v(123.7, 101.2) * mm});
            skLineSegment(sketch, "E8.11.9.0", {"start": v(123.7, 104.1) * mm, "end": v(131.7, 104.1) * mm});
            skLineSegment(sketch, "E8.11.9.1", {"start": v(131.7, 104.1) * mm, "end": v(131.7, 112.1) * mm});
            skLineSegment(sketch, "E8.11.9.2", {"start": v(123.7, 112.1) * mm, "end": v(131.7, 112.1) * mm});
            skLineSegment(sketch, "E8.11.9.3", {"start": v(123.7, 104.1) * mm, "end": v(123.7, 112.1) * mm});
            skLineSegment(sketch, "E8.11.10.0", {"start": v(123.7, 115) * mm, "end": v(131.7, 115) * mm});
            skLineSegment(sketch, "E8.11.10.1", {"start": v(131.7, 115) * mm, "end": v(131.7, 123) * mm});
            skLineSegment(sketch, "E8.11.10.2", {"start": v(123.7, 123) * mm, "end": v(131.7, 123) * mm});
            skLineSegment(sketch, "E8.11.10.3", {"start": v(123.7, 115) * mm, "end": v(123.7, 123) * mm});
            skLineSegment(sketch, "E8.11.11.0", {"start": v(123.7, 125.9) * mm, "end": v(131.7, 125.9) * mm});
            skLineSegment(sketch, "E8.11.11.1", {"start": v(131.7, 125.9) * mm, "end": v(131.7, 133.9) * mm});
            skLineSegment(sketch, "E8.11.11.2", {"start": v(123.7, 133.9) * mm, "end": v(131.7, 133.9) * mm});
            skLineSegment(sketch, "E8.11.11.3", {"start": v(123.7, 125.9) * mm, "end": v(123.7, 133.9) * mm});
            skLineSegment(sketch, "E8.12.0.0", {"start": v(134.4, 6) * mm, "end": v(142.4, 6) * mm});
            skLineSegment(sketch, "E8.12.0.1", {"start": v(142.4, 6) * mm, "end": v(142.4, 14) * mm});
            skLineSegment(sketch, "E8.12.0.2", {"start": v(134.4, 14) * mm, "end": v(142.4, 14) * mm});
            skLineSegment(sketch, "E8.12.0.3", {"start": v(134.4, 6) * mm, "end": v(134.4, 14) * mm});
            skLineSegment(sketch, "E8.12.1.0", {"start": v(134.4, 16.9) * mm, "end": v(142.4, 16.9) * mm});
            skLineSegment(sketch, "E8.12.1.1", {"start": v(142.4, 16.9) * mm, "end": v(142.4, 24.9) * mm});
            skLineSegment(sketch, "E8.12.1.2", {"start": v(134.4, 24.9) * mm, "end": v(142.4, 24.9) * mm});
            skLineSegment(sketch, "E8.12.1.3", {"start": v(134.4, 16.9) * mm, "end": v(134.4, 24.9) * mm});
            skLineSegment(sketch, "E8.12.2.0", {"start": v(134.4, 27.8) * mm, "end": v(142.4, 27.8) * mm});
            skLineSegment(sketch, "E8.12.2.1", {"start": v(142.4, 27.8) * mm, "end": v(142.4, 35.8) * mm});
            skLineSegment(sketch, "E8.12.2.2", {"start": v(134.4, 35.8) * mm, "end": v(142.4, 35.8) * mm});
            skLineSegment(sketch, "E8.12.2.3", {"start": v(134.4, 27.8) * mm, "end": v(134.4, 35.8) * mm});
            skLineSegment(sketch, "E8.12.3.0", {"start": v(134.4, 38.7) * mm, "end": v(142.4, 38.7) * mm});
            skLineSegment(sketch, "E8.12.3.1", {"start": v(142.4, 38.7) * mm, "end": v(142.4, 46.7) * mm});
            skLineSegment(sketch, "E8.12.3.2", {"start": v(134.4, 46.7) * mm, "end": v(142.4, 46.7) * mm});
            skLineSegment(sketch, "E8.12.3.3", {"start": v(134.4, 38.7) * mm, "end": v(134.4, 46.7) * mm});
            skLineSegment(sketch, "E8.12.4.0", {"start": v(134.4, 49.6) * mm, "end": v(142.4, 49.6) * mm});
            skLineSegment(sketch, "E8.12.4.1", {"start": v(142.4, 49.6) * mm, "end": v(142.4, 57.6) * mm});
            skLineSegment(sketch, "E8.12.4.2", {"start": v(134.4, 57.6) * mm, "end": v(142.4, 57.6) * mm});
            skLineSegment(sketch, "E8.12.4.3", {"start": v(134.4, 49.6) * mm, "end": v(134.4, 57.6) * mm});
            skLineSegment(sketch, "E8.12.5.0", {"start": v(134.4, 60.5) * mm, "end": v(142.4, 60.5) * mm});
            skLineSegment(sketch, "E8.12.5.1", {"start": v(142.4, 60.5) * mm, "end": v(142.4, 68.5) * mm});
            skLineSegment(sketch, "E8.12.5.2", {"start": v(134.4, 68.5) * mm, "end": v(142.4, 68.5) * mm});
            skLineSegment(sketch, "E8.12.5.3", {"start": v(134.4, 60.5) * mm, "end": v(134.4, 68.5) * mm});
            skLineSegment(sketch, "E8.12.6.0", {"start": v(134.4, 71.4) * mm, "end": v(142.4, 71.4) * mm});
            skLineSegment(sketch, "E8.12.6.1", {"start": v(142.4, 71.4) * mm, "end": v(142.4, 79.4) * mm});
            skLineSegment(sketch, "E8.12.6.2", {"start": v(134.4, 79.4) * mm, "end": v(142.4, 79.4) * mm});
            skLineSegment(sketch, "E8.12.6.3", {"start": v(134.4, 71.4) * mm, "end": v(134.4, 79.4) * mm});
            skLineSegment(sketch, "E8.12.7.0", {"start": v(134.4, 82.3) * mm, "end": v(142.4, 82.3) * mm});
            skLineSegment(sketch, "E8.12.7.1", {"start": v(142.4, 82.3) * mm, "end": v(142.4, 90.3) * mm});
            skLineSegment(sketch, "E8.12.7.2", {"start": v(134.4, 90.3) * mm, "end": v(142.4, 90.3) * mm});
            skLineSegment(sketch, "E8.12.7.3", {"start": v(134.4, 82.3) * mm, "end": v(134.4, 90.3) * mm});
            skLineSegment(sketch, "E8.12.8.0", {"start": v(134.4, 93.2) * mm, "end": v(142.4, 93.2) * mm});
            skLineSegment(sketch, "E8.12.8.1", {"start": v(142.4, 93.2) * mm, "end": v(142.4, 101.2) * mm});
            skLineSegment(sketch, "E8.12.8.2", {"start": v(134.4, 101.2) * mm, "end": v(142.4, 101.2) * mm});
            skLineSegment(sketch, "E8.12.8.3", {"start": v(134.4, 93.2) * mm, "end": v(134.4, 101.2) * mm});
            skLineSegment(sketch, "E8.12.9.0", {"start": v(134.4, 104.1) * mm, "end": v(142.4, 104.1) * mm});
            skLineSegment(sketch, "E8.12.9.1", {"start": v(142.4, 104.1) * mm, "end": v(142.4, 112.1) * mm});
            skLineSegment(sketch, "E8.12.9.2", {"start": v(134.4, 112.1) * mm, "end": v(142.4, 112.1) * mm});
            skLineSegment(sketch, "E8.12.9.3", {"start": v(134.4, 104.1) * mm, "end": v(134.4, 112.1) * mm});
            skLineSegment(sketch, "E8.12.10.0", {"start": v(134.4, 115) * mm, "end": v(142.4, 115) * mm});
            skLineSegment(sketch, "E8.12.10.1", {"start": v(142.4, 115) * mm, "end": v(142.4, 123) * mm});
            skLineSegment(sketch, "E8.12.10.2", {"start": v(134.4, 123) * mm, "end": v(142.4, 123) * mm});
            skLineSegment(sketch, "E8.12.10.3", {"start": v(134.4, 115) * mm, "end": v(134.4, 123) * mm});
            skLineSegment(sketch, "E8.12.11.0", {"start": v(134.4, 125.9) * mm, "end": v(142.4, 125.9) * mm});
            skLineSegment(sketch, "E8.12.11.1", {"start": v(142.4, 125.9) * mm, "end": v(142.4, 133.9) * mm});
            skLineSegment(sketch, "E8.12.11.2", {"start": v(134.4, 133.9) * mm, "end": v(142.4, 133.9) * mm});
            skLineSegment(sketch, "E8.12.11.3", {"start": v(134.4, 125.9) * mm, "end": v(134.4, 133.9) * mm});
            skLineSegment(sketch, "E8.13.0.0", {"start": v(145.1, 6) * mm, "end": v(153.1, 6) * mm});
            skLineSegment(sketch, "E8.13.0.1", {"start": v(153.1, 6) * mm, "end": v(153.1, 14) * mm});
            skLineSegment(sketch, "E8.13.0.2", {"start": v(145.1, 14) * mm, "end": v(153.1, 14) * mm});
            skLineSegment(sketch, "E8.13.0.3", {"start": v(145.1, 6) * mm, "end": v(145.1, 14) * mm});
            skLineSegment(sketch, "E8.13.1.0", {"start": v(145.1, 16.9) * mm, "end": v(153.1, 16.9) * mm});
            skLineSegment(sketch, "E8.13.1.1", {"start": v(153.1, 16.9) * mm, "end": v(153.1, 24.9) * mm});
            skLineSegment(sketch, "E8.13.1.2", {"start": v(145.1, 24.9) * mm, "end": v(153.1, 24.9) * mm});
            skLineSegment(sketch, "E8.13.1.3", {"start": v(145.1, 16.9) * mm, "end": v(145.1, 24.9) * mm});
            skLineSegment(sketch, "E8.13.2.0", {"start": v(145.1, 27.8) * mm, "end": v(153.1, 27.8) * mm});
            skLineSegment(sketch, "E8.13.2.1", {"start": v(153.1, 27.8) * mm, "end": v(153.1, 35.8) * mm});
            skLineSegment(sketch, "E8.13.2.2", {"start": v(145.1, 35.8) * mm, "end": v(153.1, 35.8) * mm});
            skLineSegment(sketch, "E8.13.2.3", {"start": v(145.1, 27.8) * mm, "end": v(145.1, 35.8) * mm});
            skLineSegment(sketch, "E8.13.3.0", {"start": v(145.1, 38.7) * mm, "end": v(153.1, 38.7) * mm});
            skLineSegment(sketch, "E8.13.3.1", {"start": v(153.1, 38.7) * mm, "end": v(153.1, 46.7) * mm});
            skLineSegment(sketch, "E8.13.3.2", {"start": v(145.1, 46.7) * mm, "end": v(153.1, 46.7) * mm});
            skLineSegment(sketch, "E8.13.3.3", {"start": v(145.1, 38.7) * mm, "end": v(145.1, 46.7) * mm});
            skLineSegment(sketch, "E8.13.4.0", {"start": v(145.1, 49.6) * mm, "end": v(153.1, 49.6) * mm});
            skLineSegment(sketch, "E8.13.4.1", {"start": v(153.1, 49.6) * mm, "end": v(153.1, 57.6) * mm});
            skLineSegment(sketch, "E8.13.4.2", {"start": v(145.1, 57.6) * mm, "end": v(153.1, 57.6) * mm});
            skLineSegment(sketch, "E8.13.4.3", {"start": v(145.1, 49.6) * mm, "end": v(145.1, 57.6) * mm});
            skLineSegment(sketch, "E8.13.5.0", {"start": v(145.1, 60.5) * mm, "end": v(153.1, 60.5) * mm});
            skLineSegment(sketch, "E8.13.5.1", {"start": v(153.1, 60.5) * mm, "end": v(153.1, 68.5) * mm});
            skLineSegment(sketch, "E8.13.5.2", {"start": v(145.1, 68.5) * mm, "end": v(153.1, 68.5) * mm});
            skLineSegment(sketch, "E8.13.5.3", {"start": v(145.1, 60.5) * mm, "end": v(145.1, 68.5) * mm});
            skLineSegment(sketch, "E8.13.6.0", {"start": v(145.1, 71.4) * mm, "end": v(153.1, 71.4) * mm});
            skLineSegment(sketch, "E8.13.6.1", {"start": v(153.1, 71.4) * mm, "end": v(153.1, 79.4) * mm});
            skLineSegment(sketch, "E8.13.6.2", {"start": v(145.1, 79.4) * mm, "end": v(153.1, 79.4) * mm});
            skLineSegment(sketch, "E8.13.6.3", {"start": v(145.1, 71.4) * mm, "end": v(145.1, 79.4) * mm});
            skLineSegment(sketch, "E8.13.7.0", {"start": v(145.1, 82.3) * mm, "end": v(153.1, 82.3) * mm});
            skLineSegment(sketch, "E8.13.7.1", {"start": v(153.1, 82.3) * mm, "end": v(153.1, 90.3) * mm});
            skLineSegment(sketch, "E8.13.7.2", {"start": v(145.1, 90.3) * mm, "end": v(153.1, 90.3) * mm});
            skLineSegment(sketch, "E8.13.7.3", {"start": v(145.1, 82.3) * mm, "end": v(145.1, 90.3) * mm});
            skLineSegment(sketch, "E8.13.8.0", {"start": v(145.1, 93.2) * mm, "end": v(153.1, 93.2) * mm});
            skLineSegment(sketch, "E8.13.8.1", {"start": v(153.1, 93.2) * mm, "end": v(153.1, 101.2) * mm});
            skLineSegment(sketch, "E8.13.8.2", {"start": v(145.1, 101.2) * mm, "end": v(153.1, 101.2) * mm});
            skLineSegment(sketch, "E8.13.8.3", {"start": v(145.1, 93.2) * mm, "end": v(145.1, 101.2) * mm});
            skLineSegment(sketch, "E8.13.9.0", {"start": v(145.1, 104.1) * mm, "end": v(153.1, 104.1) * mm});
            skLineSegment(sketch, "E8.13.9.1", {"start": v(153.1, 104.1) * mm, "end": v(153.1, 112.1) * mm});
            skLineSegment(sketch, "E8.13.9.2", {"start": v(145.1, 112.1) * mm, "end": v(153.1, 112.1) * mm});
            skLineSegment(sketch, "E8.13.9.3", {"start": v(145.1, 104.1) * mm, "end": v(145.1, 112.1) * mm});
            skLineSegment(sketch, "E8.13.10.0", {"start": v(145.1, 115) * mm, "end": v(153.1, 115) * mm});
            skLineSegment(sketch, "E8.13.10.1", {"start": v(153.1, 115) * mm, "end": v(153.1, 123) * mm});
            skLineSegment(sketch, "E8.13.10.2", {"start": v(145.1, 123) * mm, "end": v(153.1, 123) * mm});
            skLineSegment(sketch, "E8.13.10.3", {"start": v(145.1, 115) * mm, "end": v(145.1, 123) * mm});
            skLineSegment(sketch, "E8.13.11.0", {"start": v(145.1, 125.9) * mm, "end": v(153.1, 125.9) * mm});
            skLineSegment(sketch, "E8.13.11.1", {"start": v(153.1, 125.9) * mm, "end": v(153.1, 133.9) * mm});
            skLineSegment(sketch, "E8.13.11.2", {"start": v(145.1, 133.9) * mm, "end": v(153.1, 133.9) * mm});
            skLineSegment(sketch, "E8.13.11.3", {"start": v(145.1, 125.9) * mm, "end": v(145.1, 133.9) * mm});
            skLineSegment(sketch, "E8.14.0.0", {"start": v(155.8, 6) * mm, "end": v(163.8, 6) * mm});
            skLineSegment(sketch, "E8.14.0.1", {"start": v(163.8, 6) * mm, "end": v(163.8, 14) * mm});
            skLineSegment(sketch, "E8.14.0.2", {"start": v(155.8, 14) * mm, "end": v(163.8, 14) * mm});
            skLineSegment(sketch, "E8.14.0.3", {"start": v(155.8, 6) * mm, "end": v(155.8, 14) * mm});
            skLineSegment(sketch, "E8.14.1.0", {"start": v(155.8, 16.9) * mm, "end": v(163.8, 16.9) * mm});
            skLineSegment(sketch, "E8.14.1.1", {"start": v(163.8, 16.9) * mm, "end": v(163.8, 24.9) * mm});
            skLineSegment(sketch, "E8.14.1.2", {"start": v(155.8, 24.9) * mm, "end": v(163.8, 24.9) * mm});
            skLineSegment(sketch, "E8.14.1.3", {"start": v(155.8, 16.9) * mm, "end": v(155.8, 24.9) * mm});
            skLineSegment(sketch, "E8.14.2.0", {"start": v(155.8, 27.8) * mm, "end": v(163.8, 27.8) * mm});
            skLineSegment(sketch, "E8.14.2.1", {"start": v(163.8, 27.8) * mm, "end": v(163.8, 35.8) * mm});
            skLineSegment(sketch, "E8.14.2.2", {"start": v(155.8, 35.8) * mm, "end": v(163.8, 35.8) * mm});
            skLineSegment(sketch, "E8.14.2.3", {"start": v(155.8, 27.8) * mm, "end": v(155.8, 35.8) * mm});
            skLineSegment(sketch, "E8.14.3.0", {"start": v(155.8, 38.7) * mm, "end": v(163.8, 38.7) * mm});
            skLineSegment(sketch, "E8.14.3.1", {"start": v(163.8, 38.7) * mm, "end": v(163.8, 46.7) * mm});
            skLineSegment(sketch, "E8.14.3.2", {"start": v(155.8, 46.7) * mm, "end": v(163.8, 46.7) * mm});
            skLineSegment(sketch, "E8.14.3.3", {"start": v(155.8, 38.7) * mm, "end": v(155.8, 46.7) * mm});
            skLineSegment(sketch, "E8.14.4.0", {"start": v(155.8, 49.6) * mm, "end": v(163.8, 49.6) * mm});
            skLineSegment(sketch, "E8.14.4.1", {"start": v(163.8, 49.6) * mm, "end": v(163.8, 57.6) * mm});
            skLineSegment(sketch, "E8.14.4.2", {"start": v(155.8, 57.6) * mm, "end": v(163.8, 57.6) * mm});
            skLineSegment(sketch, "E8.14.4.3", {"start": v(155.8, 49.6) * mm, "end": v(155.8, 57.6) * mm});
            skLineSegment(sketch, "E8.14.5.0", {"start": v(155.8, 60.5) * mm, "end": v(163.8, 60.5) * mm});
            skLineSegment(sketch, "E8.14.5.1", {"start": v(163.8, 60.5) * mm, "end": v(163.8, 68.5) * mm});
            skLineSegment(sketch, "E8.14.5.2", {"start": v(155.8, 68.5) * mm, "end": v(163.8, 68.5) * mm});
            skLineSegment(sketch, "E8.14.5.3", {"start": v(155.8, 60.5) * mm, "end": v(155.8, 68.5) * mm});
            skLineSegment(sketch, "E8.14.6.0", {"start": v(155.8, 71.4) * mm, "end": v(163.8, 71.4) * mm});
            skLineSegment(sketch, "E8.14.6.1", {"start": v(163.8, 71.4) * mm, "end": v(163.8, 79.4) * mm});
            skLineSegment(sketch, "E8.14.6.2", {"start": v(155.8, 79.4) * mm, "end": v(163.8, 79.4) * mm});
            skLineSegment(sketch, "E8.14.6.3", {"start": v(155.8, 71.4) * mm, "end": v(155.8, 79.4) * mm});
            skLineSegment(sketch, "E8.14.7.0", {"start": v(155.8, 82.3) * mm, "end": v(163.8, 82.3) * mm});
            skLineSegment(sketch, "E8.14.7.1", {"start": v(163.8, 82.3) * mm, "end": v(163.8, 90.3) * mm});
            skLineSegment(sketch, "E8.14.7.2", {"start": v(155.8, 90.3) * mm, "end": v(163.8, 90.3) * mm});
            skLineSegment(sketch, "E8.14.7.3", {"start": v(155.8, 82.3) * mm, "end": v(155.8, 90.3) * mm});
            skLineSegment(sketch, "E8.14.8.0", {"start": v(155.8, 93.2) * mm, "end": v(163.8, 93.2) * mm});
            skLineSegment(sketch, "E8.14.8.1", {"start": v(163.8, 93.2) * mm, "end": v(163.8, 101.2) * mm});
            skLineSegment(sketch, "E8.14.8.2", {"start": v(155.8, 101.2) * mm, "end": v(163.8, 101.2) * mm});
            skLineSegment(sketch, "E8.14.8.3", {"start": v(155.8, 93.2) * mm, "end": v(155.8, 101.2) * mm});
            skLineSegment(sketch, "E8.14.9.0", {"start": v(155.8, 104.1) * mm, "end": v(163.8, 104.1) * mm});
            skLineSegment(sketch, "E8.14.9.1", {"start": v(163.8, 104.1) * mm, "end": v(163.8, 112.1) * mm});
            skLineSegment(sketch, "E8.14.9.2", {"start": v(155.8, 112.1) * mm, "end": v(163.8, 112.1) * mm});
            skLineSegment(sketch, "E8.14.9.3", {"start": v(155.8, 104.1) * mm, "end": v(155.8, 112.1) * mm});
            skLineSegment(sketch, "E8.14.10.0", {"start": v(155.8, 115) * mm, "end": v(163.8, 115) * mm});
            skLineSegment(sketch, "E8.14.10.1", {"start": v(163.8, 115) * mm, "end": v(163.8, 123) * mm});
            skLineSegment(sketch, "E8.14.10.2", {"start": v(155.8, 123) * mm, "end": v(163.8, 123) * mm});
            skLineSegment(sketch, "E8.14.10.3", {"start": v(155.8, 115) * mm, "end": v(155.8, 123) * mm});
            skLineSegment(sketch, "E8.14.11.0", {"start": v(155.8, 125.9) * mm, "end": v(163.8, 125.9) * mm});
            skLineSegment(sketch, "E8.14.11.1", {"start": v(163.8, 125.9) * mm, "end": v(163.8, 133.9) * mm});
            skLineSegment(sketch, "E8.14.11.2", {"start": v(155.8, 133.9) * mm, "end": v(163.8, 133.9) * mm});
            skLineSegment(sketch, "E8.14.11.3", {"start": v(155.8, 125.9) * mm, "end": v(155.8, 133.9) * mm});
            skLineSegment(sketch, "E8.direction1", {"start": v(6, 6) * mm, "end": v(16.7, 6) * mm, "construction": true});
            skLineSegment(sketch, "E8.direction2", {"start": v(6, 6) * mm, "end": v(6, 16.9) * mm, "construction": true});
            skSolve(sketch);
        }
        {
            var Q0;
            Q0=qSketchRegion(id+"F5",true);
            extrude(context, id + "F6", {"entities" : qUnion([Q0]), "operationType" : NewBodyOperationType.REMOVE, "depth" : 3 * mm, "offsetDistance" : 25 * mm});
        }
        {
            var Q0;
            Q0=makeQuery(id+"F1.opExtrude","SWEPT_FACE",FACE,{"disambiguationData":[OSD([sQuery(id+"F0.wireOp",EDGE,"E0.right")])]});
            var sketch = newSketch(context, id + "F7", { "sketchPlane" : qUnion([Q0])});
            skLineSegment(sketch, "E9.bottom", {"start": v(6, 22) * mm, "end": v(20, 22) * mm});
            skLineSegment(sketch, "E9.top", {"start": v(6, 6) * mm, "end": v(20, 6) * mm});
            skLineSegment(sketch, "E9.left", {"start": v(6, 22) * mm, "end": v(6, 6) * mm});
            skLineSegment(sketch, "E9.right", {"start": v(20, 22) * mm, "end": v(20, 6) * mm});
            skLineSegment(sketch, "E10.0.1.0", {"start": v(6, 41) * mm, "end": v(20, 41) * mm});
            skLineSegment(sketch, "E10.0.1.1", {"start": v(6, 41) * mm, "end": v(6, 25) * mm});
            skLineSegment(sketch, "E10.0.1.2", {"start": v(20, 41) * mm, "end": v(20, 25) * mm});
            skLineSegment(sketch, "E10.0.1.3", {"start": v(6, 25) * mm, "end": v(20, 25) * mm});
            skLineSegment(sketch, "E10.0.2.0", {"start": v(6, 60) * mm, "end": v(20, 60) * mm});
            skLineSegment(sketch, "E10.0.2.1", {"start": v(6, 60) * mm, "end": v(6, 44) * mm});
            skLineSegment(sketch, "E10.0.2.2", {"start": v(20, 60) * mm, "end": v(20, 44) * mm});
            skLineSegment(sketch, "E10.0.2.3", {"start": v(6, 44) * mm, "end": v(20, 44) * mm});
            skLineSegment(sketch, "E10.0.3.0", {"start": v(6, 79) * mm, "end": v(20, 79) * mm});
            skLineSegment(sketch, "E10.0.3.1", {"start": v(6, 79) * mm, "end": v(6, 63) * mm});
            skLineSegment(sketch, "E10.0.3.2", {"start": v(20, 79) * mm, "end": v(20, 63) * mm});
            skLineSegment(sketch, "E10.0.3.3", {"start": v(6, 63) * mm, "end": v(20, 63) * mm});
            skLineSegment(sketch, "E10.0.4.0", {"start": v(6, 98) * mm, "end": v(20, 98) * mm});
            skLineSegment(sketch, "E10.0.4.1", {"start": v(6, 98) * mm, "end": v(6, 82) * mm});
            skLineSegment(sketch, "E10.0.4.2", {"start": v(20, 98) * mm, "end": v(20, 82) * mm});
            skLineSegment(sketch, "E10.0.4.3", {"start": v(6, 82) * mm, "end": v(20, 82) * mm});
            skLineSegment(sketch, "E10.0.5.0", {"start": v(6, 117) * mm, "end": v(20, 117) * mm});
            skLineSegment(sketch, "E10.0.5.1", {"start": v(6, 117) * mm, "end": v(6, 101) * mm});
            skLineSegment(sketch, "E10.0.5.2", {"start": v(20, 117) * mm, "end": v(20, 101) * mm});
            skLineSegment(sketch, "E10.0.5.3", {"start": v(6, 101) * mm, "end": v(20, 101) * mm});
            skLineSegment(sketch, "E10.1.0.0", {"start": v(25, 22) * mm, "end": v(39, 22) * mm});
            skLineSegment(sketch, "E10.1.0.1", {"start": v(25, 22) * mm, "end": v(25, 6) * mm});
            skLineSegment(sketch, "E10.1.0.2", {"start": v(39, 22) * mm, "end": v(39, 6) * mm});
            skLineSegment(sketch, "E10.1.0.3", {"start": v(25, 6) * mm, "end": v(39, 6) * mm});
            skLineSegment(sketch, "E10.1.1.0", {"start": v(25, 41) * mm, "end": v(39, 41) * mm});
            skLineSegment(sketch, "E10.1.1.1", {"start": v(25, 41) * mm, "end": v(25, 25) * mm});
            skLineSegment(sketch, "E10.1.1.2", {"start": v(39, 41) * mm, "end": v(39, 25) * mm});
            skLineSegment(sketch, "E10.1.1.3", {"start": v(25, 25) * mm, "end": v(39, 25) * mm});
            skLineSegment(sketch, "E10.1.2.0", {"start": v(25, 60) * mm, "end": v(39, 60) * mm});
            skLineSegment(sketch, "E10.1.2.1", {"start": v(25, 60) * mm, "end": v(25, 44) * mm});
            skLineSegment(sketch, "E10.1.2.2", {"start": v(39, 60) * mm, "end": v(39, 44) * mm});
            skLineSegment(sketch, "E10.1.2.3", {"start": v(25, 44) * mm, "end": v(39, 44) * mm});
            skLineSegment(sketch, "E10.1.3.0", {"start": v(25, 79) * mm, "end": v(39, 79) * mm});
            skLineSegment(sketch, "E10.1.3.1", {"start": v(25, 79) * mm, "end": v(25, 63) * mm});
            skLineSegment(sketch, "E10.1.3.2", {"start": v(39, 79) * mm, "end": v(39, 63) * mm});
            skLineSegment(sketch, "E10.1.3.3", {"start": v(25, 63) * mm, "end": v(39, 63) * mm});
            skLineSegment(sketch, "E10.1.4.0", {"start": v(25, 98) * mm, "end": v(39, 98) * mm});
            skLineSegment(sketch, "E10.1.4.1", {"start": v(25, 98) * mm, "end": v(25, 82) * mm});
            skLineSegment(sketch, "E10.1.4.2", {"start": v(39, 98) * mm, "end": v(39, 82) * mm});
            skLineSegment(sketch, "E10.1.4.3", {"start": v(25, 82) * mm, "end": v(39, 82) * mm});
            skLineSegment(sketch, "E10.1.5.0", {"start": v(25, 117) * mm, "end": v(39, 117) * mm});
            skLineSegment(sketch, "E10.1.5.1", {"start": v(25, 117) * mm, "end": v(25, 101) * mm});
            skLineSegment(sketch, "E10.1.5.2", {"start": v(39, 117) * mm, "end": v(39, 101) * mm});
            skLineSegment(sketch, "E10.1.5.3", {"start": v(25, 101) * mm, "end": v(39, 101) * mm});
            skLineSegment(sketch, "E10.2.0.0", {"start": v(44, 22) * mm, "end": v(58, 22) * mm});
            skLineSegment(sketch, "E10.2.0.1", {"start": v(44, 22) * mm, "end": v(44, 6) * mm});
            skLineSegment(sketch, "E10.2.0.2", {"start": v(58, 22) * mm, "end": v(58, 6) * mm});
            skLineSegment(sketch, "E10.2.0.3", {"start": v(44, 6) * mm, "end": v(58, 6) * mm});
            skLineSegment(sketch, "E10.2.1.0", {"start": v(44, 41) * mm, "end": v(58, 41) * mm});
            skLineSegment(sketch, "E10.2.1.1", {"start": v(44, 41) * mm, "end": v(44, 25) * mm});
            skLineSegment(sketch, "E10.2.1.2", {"start": v(58, 41) * mm, "end": v(58, 25) * mm});
            skLineSegment(sketch, "E10.2.1.3", {"start": v(44, 25) * mm, "end": v(58, 25) * mm});
            skLineSegment(sketch, "E10.2.2.0", {"start": v(44, 60) * mm, "end": v(58, 60) * mm});
            skLineSegment(sketch, "E10.2.2.1", {"start": v(44, 60) * mm, "end": v(44, 44) * mm});
            skLineSegment(sketch, "E10.2.2.2", {"start": v(58, 60) * mm, "end": v(58, 44) * mm});
            skLineSegment(sketch, "E10.2.2.3", {"start": v(44, 44) * mm, "end": v(58, 44) * mm});
            skLineSegment(sketch, "E10.2.3.0", {"start": v(44, 79) * mm, "end": v(58, 79) * mm});
            skLineSegment(sketch, "E10.2.3.1", {"start": v(44, 79) * mm, "end": v(44, 63) * mm});
            skLineSegment(sketch, "E10.2.3.2", {"start": v(58, 79) * mm, "end": v(58, 63) * mm});
            skLineSegment(sketch, "E10.2.3.3", {"start": v(44, 63) * mm, "end": v(58, 63) * mm});
            skLineSegment(sketch, "E10.2.4.0", {"start": v(44, 98) * mm, "end": v(58, 98) * mm});
            skLineSegment(sketch, "E10.2.4.1", {"start": v(44, 98) * mm, "end": v(44, 82) * mm});
            skLineSegment(sketch, "E10.2.4.2", {"start": v(58, 98) * mm, "end": v(58, 82) * mm});
            skLineSegment(sketch, "E10.2.4.3", {"start": v(44, 82) * mm, "end": v(58, 82) * mm});
            skLineSegment(sketch, "E10.2.5.0", {"start": v(44, 117) * mm, "end": v(58, 117) * mm});
            skLineSegment(sketch, "E10.2.5.1", {"start": v(44, 117) * mm, "end": v(44, 101) * mm});
            skLineSegment(sketch, "E10.2.5.2", {"start": v(58, 117) * mm, "end": v(58, 101) * mm});
            skLineSegment(sketch, "E10.2.5.3", {"start": v(44, 101) * mm, "end": v(58, 101) * mm});
            skLineSegment(sketch, "E10.3.0.0", {"start": v(63, 22) * mm, "end": v(77, 22) * mm});
            skLineSegment(sketch, "E10.3.0.1", {"start": v(63, 22) * mm, "end": v(63, 6) * mm});
            skLineSegment(sketch, "E10.3.0.2", {"start": v(77, 22) * mm, "end": v(77, 6) * mm});
            skLineSegment(sketch, "E10.3.0.3", {"start": v(63, 6) * mm, "end": v(77, 6) * mm});
            skLineSegment(sketch, "E10.3.1.0", {"start": v(63, 41) * mm, "end": v(77, 41) * mm});
            skLineSegment(sketch, "E10.3.1.1", {"start": v(63, 41) * mm, "end": v(63, 25) * mm});
            skLineSegment(sketch, "E10.3.1.2", {"start": v(77, 41) * mm, "end": v(77, 25) * mm});
            skLineSegment(sketch, "E10.3.1.3", {"start": v(63, 25) * mm, "end": v(77, 25) * mm});
            skLineSegment(sketch, "E10.3.2.0", {"start": v(63, 60) * mm, "end": v(77, 60) * mm});
            skLineSegment(sketch, "E10.3.2.1", {"start": v(63, 60) * mm, "end": v(63, 44) * mm});
            skLineSegment(sketch, "E10.3.2.2", {"start": v(77, 60) * mm, "end": v(77, 44) * mm});
            skLineSegment(sketch, "E10.3.2.3", {"start": v(63, 44) * mm, "end": v(77, 44) * mm});
            skLineSegment(sketch, "E10.3.3.0", {"start": v(63, 79) * mm, "end": v(77, 79) * mm});
            skLineSegment(sketch, "E10.3.3.1", {"start": v(63, 79) * mm, "end": v(63, 63) * mm});
            skLineSegment(sketch, "E10.3.3.2", {"start": v(77, 79) * mm, "end": v(77, 63) * mm});
            skLineSegment(sketch, "E10.3.3.3", {"start": v(63, 63) * mm, "end": v(77, 63) * mm});
            skLineSegment(sketch, "E10.3.4.0", {"start": v(63, 98) * mm, "end": v(77, 98) * mm});
            skLineSegment(sketch, "E10.3.4.1", {"start": v(63, 98) * mm, "end": v(63, 82) * mm});
            skLineSegment(sketch, "E10.3.4.2", {"start": v(77, 98) * mm, "end": v(77, 82) * mm});
            skLineSegment(sketch, "E10.3.4.3", {"start": v(63, 82) * mm, "end": v(77, 82) * mm});
            skLineSegment(sketch, "E10.3.5.0", {"start": v(63, 117) * mm, "end": v(77, 117) * mm});
            skLineSegment(sketch, "E10.3.5.1", {"start": v(63, 117) * mm, "end": v(63, 101) * mm});
            skLineSegment(sketch, "E10.3.5.2", {"start": v(77, 117) * mm, "end": v(77, 101) * mm});
            skLineSegment(sketch, "E10.3.5.3", {"start": v(63, 101) * mm, "end": v(77, 101) * mm});
            skLineSegment(sketch, "E10.4.0.0", {"start": v(82, 22) * mm, "end": v(96, 22) * mm});
            skLineSegment(sketch, "E10.4.0.1", {"start": v(82, 22) * mm, "end": v(82, 6) * mm});
            skLineSegment(sketch, "E10.4.0.2", {"start": v(96, 22) * mm, "end": v(96, 6) * mm});
            skLineSegment(sketch, "E10.4.0.3", {"start": v(82, 6) * mm, "end": v(96, 6) * mm});
            skLineSegment(sketch, "E10.4.1.0", {"start": v(82, 41) * mm, "end": v(96, 41) * mm});
            skLineSegment(sketch, "E10.4.1.1", {"start": v(82, 41) * mm, "end": v(82, 25) * mm});
            skLineSegment(sketch, "E10.4.1.2", {"start": v(96, 41) * mm, "end": v(96, 25) * mm});
            skLineSegment(sketch, "E10.4.1.3", {"start": v(82, 25) * mm, "end": v(96, 25) * mm});
            skLineSegment(sketch, "E10.4.2.0", {"start": v(82, 60) * mm, "end": v(96, 60) * mm});
            skLineSegment(sketch, "E10.4.2.1", {"start": v(82, 60) * mm, "end": v(82, 44) * mm});
            skLineSegment(sketch, "E10.4.2.2", {"start": v(96, 60) * mm, "end": v(96, 44) * mm});
            skLineSegment(sketch, "E10.4.2.3", {"start": v(82, 44) * mm, "end": v(96, 44) * mm});
            skLineSegment(sketch, "E10.4.3.0", {"start": v(82, 79) * mm, "end": v(96, 79) * mm});
            skLineSegment(sketch, "E10.4.3.1", {"start": v(82, 79) * mm, "end": v(82, 63) * mm});
            skLineSegment(sketch, "E10.4.3.2", {"start": v(96, 79) * mm, "end": v(96, 63) * mm});
            skLineSegment(sketch, "E10.4.3.3", {"start": v(82, 63) * mm, "end": v(96, 63) * mm});
            skLineSegment(sketch, "E10.4.4.0", {"start": v(82, 98) * mm, "end": v(96, 98) * mm});
            skLineSegment(sketch, "E10.4.4.1", {"start": v(82, 98) * mm, "end": v(82, 82) * mm});
            skLineSegment(sketch, "E10.4.4.2", {"start": v(96, 98) * mm, "end": v(96, 82) * mm});
            skLineSegment(sketch, "E10.4.4.3", {"start": v(82, 82) * mm, "end": v(96, 82) * mm});
            skLineSegment(sketch, "E10.4.5.0", {"start": v(82, 117) * mm, "end": v(96, 117) * mm});
            skLineSegment(sketch, "E10.4.5.1", {"start": v(82, 117) * mm, "end": v(82, 101) * mm});
            skLineSegment(sketch, "E10.4.5.2", {"start": v(96, 117) * mm, "end": v(96, 101) * mm});
            skLineSegment(sketch, "E10.4.5.3", {"start": v(82, 101) * mm, "end": v(96, 101) * mm});
            skLineSegment(sketch, "E10.5.0.0", {"start": v(101, 22) * mm, "end": v(115, 22) * mm});
            skLineSegment(sketch, "E10.5.0.1", {"start": v(101, 22) * mm, "end": v(101, 6) * mm});
            skLineSegment(sketch, "E10.5.0.2", {"start": v(115, 22) * mm, "end": v(115, 6) * mm});
            skLineSegment(sketch, "E10.5.0.3", {"start": v(101, 6) * mm, "end": v(115, 6) * mm});
            skLineSegment(sketch, "E10.5.1.0", {"start": v(101, 41) * mm, "end": v(115, 41) * mm});
            skLineSegment(sketch, "E10.5.1.1", {"start": v(101, 41) * mm, "end": v(101, 25) * mm});
            skLineSegment(sketch, "E10.5.1.2", {"start": v(115, 41) * mm, "end": v(115, 25) * mm});
            skLineSegment(sketch, "E10.5.1.3", {"start": v(101, 25) * mm, "end": v(115, 25) * mm});
            skLineSegment(sketch, "E10.5.2.0", {"start": v(101, 60) * mm, "end": v(115, 60) * mm});
            skLineSegment(sketch, "E10.5.2.1", {"start": v(101, 60) * mm, "end": v(101, 44) * mm});
            skLineSegment(sketch, "E10.5.2.2", {"start": v(115, 60) * mm, "end": v(115, 44) * mm});
            skLineSegment(sketch, "E10.5.2.3", {"start": v(101, 44) * mm, "end": v(115, 44) * mm});
            skLineSegment(sketch, "E10.5.3.0", {"start": v(101, 79) * mm, "end": v(115, 79) * mm});
            skLineSegment(sketch, "E10.5.3.1", {"start": v(101, 79) * mm, "end": v(101, 63) * mm});
            skLineSegment(sketch, "E10.5.3.2", {"start": v(115, 79) * mm, "end": v(115, 63) * mm});
            skLineSegment(sketch, "E10.5.3.3", {"start": v(101, 63) * mm, "end": v(115, 63) * mm});
            skLineSegment(sketch, "E10.5.4.0", {"start": v(101, 98) * mm, "end": v(115, 98) * mm});
            skLineSegment(sketch, "E10.5.4.1", {"start": v(101, 98) * mm, "end": v(101, 82) * mm});
            skLineSegment(sketch, "E10.5.4.2", {"start": v(115, 98) * mm, "end": v(115, 82) * mm});
            skLineSegment(sketch, "E10.5.4.3", {"start": v(101, 82) * mm, "end": v(115, 82) * mm});
            skLineSegment(sketch, "E10.5.5.0", {"start": v(101, 117) * mm, "end": v(115, 117) * mm});
            skLineSegment(sketch, "E10.5.5.1", {"start": v(101, 117) * mm, "end": v(101, 101) * mm});
            skLineSegment(sketch, "E10.5.5.2", {"start": v(115, 117) * mm, "end": v(115, 101) * mm});
            skLineSegment(sketch, "E10.5.5.3", {"start": v(101, 101) * mm, "end": v(115, 101) * mm});
            skLineSegment(sketch, "E10.6.0.0", {"start": v(120, 22) * mm, "end": v(134, 22) * mm});
            skLineSegment(sketch, "E10.6.0.1", {"start": v(120, 22) * mm, "end": v(120, 6) * mm});
            skLineSegment(sketch, "E10.6.0.2", {"start": v(134, 22) * mm, "end": v(134, 6) * mm});
            skLineSegment(sketch, "E10.6.0.3", {"start": v(120, 6) * mm, "end": v(134, 6) * mm});
            skLineSegment(sketch, "E10.6.1.0", {"start": v(120, 41) * mm, "end": v(134, 41) * mm});
            skLineSegment(sketch, "E10.6.1.1", {"start": v(120, 41) * mm, "end": v(120, 25) * mm});
            skLineSegment(sketch, "E10.6.1.2", {"start": v(134, 41) * mm, "end": v(134, 25) * mm});
            skLineSegment(sketch, "E10.6.1.3", {"start": v(120, 25) * mm, "end": v(134, 25) * mm});
            skLineSegment(sketch, "E10.6.2.0", {"start": v(120, 60) * mm, "end": v(134, 60) * mm});
            skLineSegment(sketch, "E10.6.2.1", {"start": v(120, 60) * mm, "end": v(120, 44) * mm});
            skLineSegment(sketch, "E10.6.2.2", {"start": v(134, 60) * mm, "end": v(134, 44) * mm});
            skLineSegment(sketch, "E10.6.2.3", {"start": v(120, 44) * mm, "end": v(134, 44) * mm});
            skLineSegment(sketch, "E10.6.3.0", {"start": v(120, 79) * mm, "end": v(134, 79) * mm});
            skLineSegment(sketch, "E10.6.3.1", {"start": v(120, 79) * mm, "end": v(120, 63) * mm});
            skLineSegment(sketch, "E10.6.3.2", {"start": v(134, 79) * mm, "end": v(134, 63) * mm});
            skLineSegment(sketch, "E10.6.3.3", {"start": v(120, 63) * mm, "end": v(134, 63) * mm});
            skLineSegment(sketch, "E10.6.4.0", {"start": v(120, 98) * mm, "end": v(134, 98) * mm});
            skLineSegment(sketch, "E10.6.4.1", {"start": v(120, 98) * mm, "end": v(120, 82) * mm});
            skLineSegment(sketch, "E10.6.4.2", {"start": v(134, 98) * mm, "end": v(134, 82) * mm});
            skLineSegment(sketch, "E10.6.4.3", {"start": v(120, 82) * mm, "end": v(134, 82) * mm});
            skLineSegment(sketch, "E10.6.5.0", {"start": v(120, 117) * mm, "end": v(134, 117) * mm});
            skLineSegment(sketch, "E10.6.5.1", {"start": v(120, 117) * mm, "end": v(120, 101) * mm});
            skLineSegment(sketch, "E10.6.5.2", {"start": v(134, 117) * mm, "end": v(134, 101) * mm});
            skLineSegment(sketch, "E10.6.5.3", {"start": v(120, 101) * mm, "end": v(134, 101) * mm});
            skLineSegment(sketch, "E10.direction1", {"start": v(6, 6) * mm, "end": v(25, 6) * mm, "construction": true});
            skLineSegment(sketch, "E10.direction2", {"start": v(6, 6) * mm, "end": v(6, 25) * mm, "construction": true});
            skLineSegment(sketch, "E11", {"start": v(134, 0) * mm, "end": v(134, 49.45) * mm, "construction": true});
            skSolve(sketch);
        }
        {
            var Q0;
            Q0 = qSketchRegion(id + "F7", true);
            extrude(context, id + "F8", {"entities" : qUnion([Q0]), "operationType" : NewBodyOperationType.REMOVE, "oppositeDirection" : true, "depth" : 170 * mm, "offsetDistance" : 25 * mm});
        }
        {
            var Q0;
            Q0=makeQuery(id+"F1.opExtrude","SWEPT_FACE",FACE,{"disambiguationData":[OSD([sQuery(id+"F0.wireOp",EDGE,"E0.bottom")])]});
            var sketch = newSketch(context, id + "F9", { "sketchPlane" : qUnion([Q0])});
            skLineSegment(sketch, "E12.bottom", {"start": v(6, 22) * mm, "end": v(21.5, 22) * mm});
            skLineSegment(sketch, "E12.top", {"start": v(6, 6) * mm, "end": v(21.5, 6) * mm});
            skLineSegment(sketch, "E12.left", {"start": v(6, 22) * mm, "end": v(6, 6) * mm});
            skLineSegment(sketch, "E12.right", {"start": v(21.5, 22) * mm, "end": v(21.5, 6) * mm});
            skLineSegment(sketch, "E13.0.1.0", {"start": v(6, 41) * mm, "end": v(6, 25) * mm});
            skLineSegment(sketch, "E13.0.1.1", {"start": v(21.5, 41) * mm, "end": v(21.5, 25) * mm});
            skLineSegment(sketch, "E13.0.1.2", {"start": v(6, 41) * mm, "end": v(21.5, 41) * mm});
            skLineSegment(sketch, "E13.0.1.3", {"start": v(6, 25) * mm, "end": v(21.5, 25) * mm});
            skLineSegment(sketch, "E13.0.2.0", {"start": v(6, 60) * mm, "end": v(6, 44) * mm});
            skLineSegment(sketch, "E13.0.2.1", {"start": v(21.5, 60) * mm, "end": v(21.5, 44) * mm});
            skLineSegment(sketch, "E13.0.2.2", {"start": v(6, 60) * mm, "end": v(21.5, 60) * mm});
            skLineSegment(sketch, "E13.0.2.3", {"start": v(6, 44) * mm, "end": v(21.5, 44) * mm});
            skLineSegment(sketch, "E13.0.3.0", {"start": v(6, 79) * mm, "end": v(6, 63) * mm});
            skLineSegment(sketch, "E13.0.3.1", {"start": v(21.5, 79) * mm, "end": v(21.5, 63) * mm});
            skLineSegment(sketch, "E13.0.3.2", {"start": v(6, 79) * mm, "end": v(21.5, 79) * mm});
            skLineSegment(sketch, "E13.0.3.3", {"start": v(6, 63) * mm, "end": v(21.5, 63) * mm});
            skLineSegment(sketch, "E13.0.4.0", {"start": v(6, 98) * mm, "end": v(6, 82) * mm});
            skLineSegment(sketch, "E13.0.4.1", {"start": v(21.5, 98) * mm, "end": v(21.5, 82) * mm});
            skLineSegment(sketch, "E13.0.4.2", {"start": v(6, 98) * mm, "end": v(21.5, 98) * mm});
            skLineSegment(sketch, "E13.0.4.3", {"start": v(6, 82) * mm, "end": v(21.5, 82) * mm});
            skLineSegment(sketch, "E13.0.5.0", {"start": v(6, 117) * mm, "end": v(6, 101) * mm});
            skLineSegment(sketch, "E13.0.5.1", {"start": v(21.5, 117) * mm, "end": v(21.5, 101) * mm});
            skLineSegment(sketch, "E13.0.5.2", {"start": v(6, 117) * mm, "end": v(21.5, 117) * mm});
            skLineSegment(sketch, "E13.0.5.3", {"start": v(6, 101) * mm, "end": v(21.5, 101) * mm});
            skLineSegment(sketch, "E13.1.0.0", {"start": v(23.6, 22) * mm, "end": v(23.6, 6) * mm});
            skLineSegment(sketch, "E13.1.0.1", {"start": v(39.1, 22) * mm, "end": v(39.1, 6) * mm});
            skLineSegment(sketch, "E13.1.0.2", {"start": v(23.6, 22) * mm, "end": v(39.1, 22) * mm});
            skLineSegment(sketch, "E13.1.0.3", {"start": v(23.6, 6) * mm, "end": v(39.1, 6) * mm});
            skLineSegment(sketch, "E13.1.1.0", {"start": v(23.6, 41) * mm, "end": v(23.6, 25) * mm});
            skLineSegment(sketch, "E13.1.1.1", {"start": v(39.1, 41) * mm, "end": v(39.1, 25) * mm});
            skLineSegment(sketch, "E13.1.1.2", {"start": v(23.6, 41) * mm, "end": v(39.1, 41) * mm});
            skLineSegment(sketch, "E13.1.1.3", {"start": v(23.6, 25) * mm, "end": v(39.1, 25) * mm});
            skLineSegment(sketch, "E13.1.2.0", {"start": v(23.6, 60) * mm, "end": v(23.6, 44) * mm});
            skLineSegment(sketch, "E13.1.2.1", {"start": v(39.1, 60) * mm, "end": v(39.1, 44) * mm});
            skLineSegment(sketch, "E13.1.2.2", {"start": v(23.6, 60) * mm, "end": v(39.1, 60) * mm});
            skLineSegment(sketch, "E13.1.2.3", {"start": v(23.6, 44) * mm, "end": v(39.1, 44) * mm});
            skLineSegment(sketch, "E13.1.3.0", {"start": v(23.6, 79) * mm, "end": v(23.6, 63) * mm});
            skLineSegment(sketch, "E13.1.3.1", {"start": v(39.1, 79) * mm, "end": v(39.1, 63) * mm});
            skLineSegment(sketch, "E13.1.3.2", {"start": v(23.6, 79) * mm, "end": v(39.1, 79) * mm});
            skLineSegment(sketch, "E13.1.3.3", {"start": v(23.6, 63) * mm, "end": v(39.1, 63) * mm});
            skLineSegment(sketch, "E13.1.4.0", {"start": v(23.6, 98) * mm, "end": v(23.6, 82) * mm});
            skLineSegment(sketch, "E13.1.4.1", {"start": v(39.1, 98) * mm, "end": v(39.1, 82) * mm});
            skLineSegment(sketch, "E13.1.4.2", {"start": v(23.6, 98) * mm, "end": v(39.1, 98) * mm});
            skLineSegment(sketch, "E13.1.4.3", {"start": v(23.6, 82) * mm, "end": v(39.1, 82) * mm});
            skLineSegment(sketch, "E13.1.5.0", {"start": v(23.6, 117) * mm, "end": v(23.6, 101) * mm});
            skLineSegment(sketch, "E13.1.5.1", {"start": v(39.1, 117) * mm, "end": v(39.1, 101) * mm});
            skLineSegment(sketch, "E13.1.5.2", {"start": v(23.6, 117) * mm, "end": v(39.1, 117) * mm});
            skLineSegment(sketch, "E13.1.5.3", {"start": v(23.6, 101) * mm, "end": v(39.1, 101) * mm});
            skLineSegment(sketch, "E13.2.0.0", {"start": v(41.2, 22) * mm, "end": v(41.2, 6) * mm});
            skLineSegment(sketch, "E13.2.0.1", {"start": v(56.7, 22) * mm, "end": v(56.7, 6) * mm});
            skLineSegment(sketch, "E13.2.0.2", {"start": v(41.2, 22) * mm, "end": v(56.7, 22) * mm});
            skLineSegment(sketch, "E13.2.0.3", {"start": v(41.2, 6) * mm, "end": v(56.7, 6) * mm});
            skLineSegment(sketch, "E13.2.1.0", {"start": v(41.2, 41) * mm, "end": v(41.2, 25) * mm});
            skLineSegment(sketch, "E13.2.1.1", {"start": v(56.7, 41) * mm, "end": v(56.7, 25) * mm});
            skLineSegment(sketch, "E13.2.1.2", {"start": v(41.2, 41) * mm, "end": v(56.7, 41) * mm});
            skLineSegment(sketch, "E13.2.1.3", {"start": v(41.2, 25) * mm, "end": v(56.7, 25) * mm});
            skLineSegment(sketch, "E13.2.2.0", {"start": v(41.2, 60) * mm, "end": v(41.2, 44) * mm});
            skLineSegment(sketch, "E13.2.2.1", {"start": v(56.7, 60) * mm, "end": v(56.7, 44) * mm});
            skLineSegment(sketch, "E13.2.2.2", {"start": v(41.2, 60) * mm, "end": v(56.7, 60) * mm});
            skLineSegment(sketch, "E13.2.2.3", {"start": v(41.2, 44) * mm, "end": v(56.7, 44) * mm});
            skLineSegment(sketch, "E13.2.3.0", {"start": v(41.2, 79) * mm, "end": v(41.2, 63) * mm});
            skLineSegment(sketch, "E13.2.3.1", {"start": v(56.7, 79) * mm, "end": v(56.7, 63) * mm});
            skLineSegment(sketch, "E13.2.3.2", {"start": v(41.2, 79) * mm, "end": v(56.7, 79) * mm});
            skLineSegment(sketch, "E13.2.3.3", {"start": v(41.2, 63) * mm, "end": v(56.7, 63) * mm});
            skLineSegment(sketch, "E13.2.4.0", {"start": v(41.2, 98) * mm, "end": v(41.2, 82) * mm});
            skLineSegment(sketch, "E13.2.4.1", {"start": v(56.7, 98) * mm, "end": v(56.7, 82) * mm});
            skLineSegment(sketch, "E13.2.4.2", {"start": v(41.2, 98) * mm, "end": v(56.7, 98) * mm});
            skLineSegment(sketch, "E13.2.4.3", {"start": v(41.2, 82) * mm, "end": v(56.7, 82) * mm});
            skLineSegment(sketch, "E13.2.5.0", {"start": v(41.2, 117) * mm, "end": v(41.2, 101) * mm});
            skLineSegment(sketch, "E13.2.5.1", {"start": v(56.7, 117) * mm, "end": v(56.7, 101) * mm});
            skLineSegment(sketch, "E13.2.5.2", {"start": v(41.2, 117) * mm, "end": v(56.7, 117) * mm});
            skLineSegment(sketch, "E13.2.5.3", {"start": v(41.2, 101) * mm, "end": v(56.7, 101) * mm});
            skLineSegment(sketch, "E13.direction1", {"start": v(6, 6) * mm, "end": v(23.6, 6) * mm, "construction": true});
            skLineSegment(sketch, "E13.direction2", {"start": v(6, 6) * mm, "end": v(6, 25) * mm, "construction": true});
            skLineSegment(sketch, "E14", {"start": v(164, 0) * mm, "end": v(164, 59.25) * mm, "construction": true});
            skLineSegment(sketch, "E15.0.3.0", {"start": v(58.8, 22) * mm, "end": v(58.8, 6) * mm});
            skLineSegment(sketch, "E15.3.3.0", {"start": v(74.3, 22) * mm, "end": v(74.3, 6) * mm});
            skLineSegment(sketch, "E15.6.3.0", {"start": v(58.8, 22) * mm, "end": v(74.3, 22) * mm});
            skLineSegment(sketch, "E15.9.3.0", {"start": v(58.8, 6) * mm, "end": v(74.3, 6) * mm});
            skLineSegment(sketch, "E15.0.3.1", {"start": v(58.8, 41) * mm, "end": v(58.8, 25) * mm});
            skLineSegment(sketch, "E15.3.3.1", {"start": v(74.3, 41) * mm, "end": v(74.3, 25) * mm});
            skLineSegment(sketch, "E15.6.3.1", {"start": v(58.8, 41) * mm, "end": v(74.3, 41) * mm});
            skLineSegment(sketch, "E15.9.3.1", {"start": v(58.8, 25) * mm, "end": v(74.3, 25) * mm});
            skLineSegment(sketch, "E15.0.3.2", {"start": v(58.8, 60) * mm, "end": v(58.8, 44) * mm});
            skLineSegment(sketch, "E15.3.3.2", {"start": v(74.3, 60) * mm, "end": v(74.3, 44) * mm});
            skLineSegment(sketch, "E15.6.3.2", {"start": v(58.8, 60) * mm, "end": v(74.3, 60) * mm});
            skLineSegment(sketch, "E15.9.3.2", {"start": v(58.8, 44) * mm, "end": v(74.3, 44) * mm});
            skLineSegment(sketch, "E15.0.3.3", {"start": v(58.8, 79) * mm, "end": v(58.8, 63) * mm});
            skLineSegment(sketch, "E15.3.3.3", {"start": v(74.3, 79) * mm, "end": v(74.3, 63) * mm});
            skLineSegment(sketch, "E15.6.3.3", {"start": v(58.8, 79) * mm, "end": v(74.3, 79) * mm});
            skLineSegment(sketch, "E15.9.3.3", {"start": v(58.8, 63) * mm, "end": v(74.3, 63) * mm});
            skLineSegment(sketch, "E15.0.3.4", {"start": v(58.8, 98) * mm, "end": v(58.8, 82) * mm});
            skLineSegment(sketch, "E15.3.3.4", {"start": v(74.3, 98) * mm, "end": v(74.3, 82) * mm});
            skLineSegment(sketch, "E15.6.3.4", {"start": v(58.8, 98) * mm, "end": v(74.3, 98) * mm});
            skLineSegment(sketch, "E15.9.3.4", {"start": v(58.8, 82) * mm, "end": v(74.3, 82) * mm});
            skLineSegment(sketch, "E15.0.3.5", {"start": v(58.8, 117) * mm, "end": v(58.8, 101) * mm});
            skLineSegment(sketch, "E15.3.3.5", {"start": v(74.3, 117) * mm, "end": v(74.3, 101) * mm});
            skLineSegment(sketch, "E15.6.3.5", {"start": v(58.8, 117) * mm, "end": v(74.3, 117) * mm});
            skLineSegment(sketch, "E15.9.3.5", {"start": v(58.8, 101) * mm, "end": v(74.3, 101) * mm});
            skLineSegment(sketch, "E15.0.4.0", {"start": v(76.4, 22) * mm, "end": v(76.4, 6) * mm});
            skLineSegment(sketch, "E15.3.4.0", {"start": v(91.9, 22) * mm, "end": v(91.9, 6) * mm});
            skLineSegment(sketch, "E15.6.4.0", {"start": v(76.4, 22) * mm, "end": v(91.9, 22) * mm});
            skLineSegment(sketch, "E15.9.4.0", {"start": v(76.4, 6) * mm, "end": v(91.9, 6) * mm});
            skLineSegment(sketch, "E15.0.4.1", {"start": v(76.4, 41) * mm, "end": v(76.4, 25) * mm});
            skLineSegment(sketch, "E15.3.4.1", {"start": v(91.9, 41) * mm, "end": v(91.9, 25) * mm});
            skLineSegment(sketch, "E15.6.4.1", {"start": v(76.4, 41) * mm, "end": v(91.9, 41) * mm});
            skLineSegment(sketch, "E15.9.4.1", {"start": v(76.4, 25) * mm, "end": v(91.9, 25) * mm});
            skLineSegment(sketch, "E15.0.4.2", {"start": v(76.4, 60) * mm, "end": v(76.4, 44) * mm});
            skLineSegment(sketch, "E15.3.4.2", {"start": v(91.9, 60) * mm, "end": v(91.9, 44) * mm});
            skLineSegment(sketch, "E15.6.4.2", {"start": v(76.4, 60) * mm, "end": v(91.9, 60) * mm});
            skLineSegment(sketch, "E15.9.4.2", {"start": v(76.4, 44) * mm, "end": v(91.9, 44) * mm});
            skLineSegment(sketch, "E15.0.4.3", {"start": v(76.4, 79) * mm, "end": v(76.4, 63) * mm});
            skLineSegment(sketch, "E15.3.4.3", {"start": v(91.9, 79) * mm, "end": v(91.9, 63) * mm});
            skLineSegment(sketch, "E15.6.4.3", {"start": v(76.4, 79) * mm, "end": v(91.9, 79) * mm});
            skLineSegment(sketch, "E15.9.4.3", {"start": v(76.4, 63) * mm, "end": v(91.9, 63) * mm});
            skLineSegment(sketch, "E15.0.4.4", {"start": v(76.4, 98) * mm, "end": v(76.4, 82) * mm});
            skLineSegment(sketch, "E15.3.4.4", {"start": v(91.9, 98) * mm, "end": v(91.9, 82) * mm});
            skLineSegment(sketch, "E15.6.4.4", {"start": v(76.4, 98) * mm, "end": v(91.9, 98) * mm});
            skLineSegment(sketch, "E15.9.4.4", {"start": v(76.4, 82) * mm, "end": v(91.9, 82) * mm});
            skLineSegment(sketch, "E15.0.4.5", {"start": v(76.4, 117) * mm, "end": v(76.4, 101) * mm});
            skLineSegment(sketch, "E15.3.4.5", {"start": v(91.9, 117) * mm, "end": v(91.9, 101) * mm});
            skLineSegment(sketch, "E15.6.4.5", {"start": v(76.4, 117) * mm, "end": v(91.9, 117) * mm});
            skLineSegment(sketch, "E15.9.4.5", {"start": v(76.4, 101) * mm, "end": v(91.9, 101) * mm});
            skLineSegment(sketch, "E15.0.5.0", {"start": v(94, 22) * mm, "end": v(94, 6) * mm});
            skLineSegment(sketch, "E15.3.5.0", {"start": v(109.5, 22) * mm, "end": v(109.5, 6) * mm});
            skLineSegment(sketch, "E15.6.5.0", {"start": v(94, 22) * mm, "end": v(109.5, 22) * mm});
            skLineSegment(sketch, "E15.9.5.0", {"start": v(94, 6) * mm, "end": v(109.5, 6) * mm});
            skLineSegment(sketch, "E15.0.5.1", {"start": v(94, 41) * mm, "end": v(94, 25) * mm});
            skLineSegment(sketch, "E15.3.5.1", {"start": v(109.5, 41) * mm, "end": v(109.5, 25) * mm});
            skLineSegment(sketch, "E15.6.5.1", {"start": v(94, 41) * mm, "end": v(109.5, 41) * mm});
            skLineSegment(sketch, "E15.9.5.1", {"start": v(94, 25) * mm, "end": v(109.5, 25) * mm});
            skLineSegment(sketch, "E15.0.5.2", {"start": v(94, 60) * mm, "end": v(94, 44) * mm});
            skLineSegment(sketch, "E15.3.5.2", {"start": v(109.5, 60) * mm, "end": v(109.5, 44) * mm});
            skLineSegment(sketch, "E15.6.5.2", {"start": v(94, 60) * mm, "end": v(109.5, 60) * mm});
            skLineSegment(sketch, "E15.9.5.2", {"start": v(94, 44) * mm, "end": v(109.5, 44) * mm});
            skLineSegment(sketch, "E15.0.5.3", {"start": v(94, 79) * mm, "end": v(94, 63) * mm});
            skLineSegment(sketch, "E15.3.5.3", {"start": v(109.5, 79) * mm, "end": v(109.5, 63) * mm});
            skLineSegment(sketch, "E15.6.5.3", {"start": v(94, 79) * mm, "end": v(109.5, 79) * mm});
            skLineSegment(sketch, "E15.9.5.3", {"start": v(94, 63) * mm, "end": v(109.5, 63) * mm});
            skLineSegment(sketch, "E15.0.5.4", {"start": v(94, 98) * mm, "end": v(94, 82) * mm});
            skLineSegment(sketch, "E15.3.5.4", {"start": v(109.5, 98) * mm, "end": v(109.5, 82) * mm});
            skLineSegment(sketch, "E15.6.5.4", {"start": v(94, 98) * mm, "end": v(109.5, 98) * mm});
            skLineSegment(sketch, "E15.9.5.4", {"start": v(94, 82) * mm, "end": v(109.5, 82) * mm});
            skLineSegment(sketch, "E15.0.5.5", {"start": v(94, 117) * mm, "end": v(94, 101) * mm});
            skLineSegment(sketch, "E15.3.5.5", {"start": v(109.5, 117) * mm, "end": v(109.5, 101) * mm});
            skLineSegment(sketch, "E15.6.5.5", {"start": v(94, 117) * mm, "end": v(109.5, 117) * mm});
            skLineSegment(sketch, "E15.9.5.5", {"start": v(94, 101) * mm, "end": v(109.5, 101) * mm});
            skLineSegment(sketch, "E15.0.6.0", {"start": v(111.6, 22) * mm, "end": v(111.6, 6) * mm});
            skLineSegment(sketch, "E15.3.6.0", {"start": v(127.1, 22) * mm, "end": v(127.1, 6) * mm});
            skLineSegment(sketch, "E15.6.6.0", {"start": v(111.6, 22) * mm, "end": v(127.1, 22) * mm});
            skLineSegment(sketch, "E15.9.6.0", {"start": v(111.6, 6) * mm, "end": v(127.1, 6) * mm});
            skLineSegment(sketch, "E15.0.6.1", {"start": v(111.6, 41) * mm, "end": v(111.6, 25) * mm});
            skLineSegment(sketch, "E15.3.6.1", {"start": v(127.1, 41) * mm, "end": v(127.1, 25) * mm});
            skLineSegment(sketch, "E15.6.6.1", {"start": v(111.6, 41) * mm, "end": v(127.1, 41) * mm});
            skLineSegment(sketch, "E15.9.6.1", {"start": v(111.6, 25) * mm, "end": v(127.1, 25) * mm});
            skLineSegment(sketch, "E15.0.6.2", {"start": v(111.6, 60) * mm, "end": v(111.6, 44) * mm});
            skLineSegment(sketch, "E15.3.6.2", {"start": v(127.1, 60) * mm, "end": v(127.1, 44) * mm});
            skLineSegment(sketch, "E15.6.6.2", {"start": v(111.6, 60) * mm, "end": v(127.1, 60) * mm});
            skLineSegment(sketch, "E15.9.6.2", {"start": v(111.6, 44) * mm, "end": v(127.1, 44) * mm});
            skLineSegment(sketch, "E15.0.6.3", {"start": v(111.6, 79) * mm, "end": v(111.6, 63) * mm});
            skLineSegment(sketch, "E15.3.6.3", {"start": v(127.1, 79) * mm, "end": v(127.1, 63) * mm});
            skLineSegment(sketch, "E15.6.6.3", {"start": v(111.6, 79) * mm, "end": v(127.1, 79) * mm});
            skLineSegment(sketch, "E15.9.6.3", {"start": v(111.6, 63) * mm, "end": v(127.1, 63) * mm});
            skLineSegment(sketch, "E15.0.6.4", {"start": v(111.6, 98) * mm, "end": v(111.6, 82) * mm});
            skLineSegment(sketch, "E15.3.6.4", {"start": v(127.1, 98) * mm, "end": v(127.1, 82) * mm});
            skLineSegment(sketch, "E15.6.6.4", {"start": v(111.6, 98) * mm, "end": v(127.1, 98) * mm});
            skLineSegment(sketch, "E15.9.6.4", {"start": v(111.6, 82) * mm, "end": v(127.1, 82) * mm});
            skLineSegment(sketch, "E15.0.6.5", {"start": v(111.6, 117) * mm, "end": v(111.6, 101) * mm});
            skLineSegment(sketch, "E15.3.6.5", {"start": v(127.1, 117) * mm, "end": v(127.1, 101) * mm});
            skLineSegment(sketch, "E15.6.6.5", {"start": v(111.6, 117) * mm, "end": v(127.1, 117) * mm});
            skLineSegment(sketch, "E15.9.6.5", {"start": v(111.6, 101) * mm, "end": v(127.1, 101) * mm});
            skLineSegment(sketch, "E15.0.7.0", {"start": v(129.2, 22) * mm, "end": v(129.2, 6) * mm});
            skLineSegment(sketch, "E15.3.7.0", {"start": v(144.7, 22) * mm, "end": v(144.7, 6) * mm});
            skLineSegment(sketch, "E15.6.7.0", {"start": v(129.2, 22) * mm, "end": v(144.7, 22) * mm});
            skLineSegment(sketch, "E15.9.7.0", {"start": v(129.2, 6) * mm, "end": v(144.7, 6) * mm});
            skLineSegment(sketch, "E15.0.7.1", {"start": v(129.2, 41) * mm, "end": v(129.2, 25) * mm});
            skLineSegment(sketch, "E15.3.7.1", {"start": v(144.7, 41) * mm, "end": v(144.7, 25) * mm});
            skLineSegment(sketch, "E15.6.7.1", {"start": v(129.2, 41) * mm, "end": v(144.7, 41) * mm});
            skLineSegment(sketch, "E15.9.7.1", {"start": v(129.2, 25) * mm, "end": v(144.7, 25) * mm});
            skLineSegment(sketch, "E15.0.7.2", {"start": v(129.2, 60) * mm, "end": v(129.2, 44) * mm});
            skLineSegment(sketch, "E15.3.7.2", {"start": v(144.7, 60) * mm, "end": v(144.7, 44) * mm});
            skLineSegment(sketch, "E15.6.7.2", {"start": v(129.2, 60) * mm, "end": v(144.7, 60) * mm});
            skLineSegment(sketch, "E15.9.7.2", {"start": v(129.2, 44) * mm, "end": v(144.7, 44) * mm});
            skLineSegment(sketch, "E15.0.7.3", {"start": v(129.2, 79) * mm, "end": v(129.2, 63) * mm});
            skLineSegment(sketch, "E15.3.7.3", {"start": v(144.7, 79) * mm, "end": v(144.7, 63) * mm});
            skLineSegment(sketch, "E15.6.7.3", {"start": v(129.2, 79) * mm, "end": v(144.7, 79) * mm});
            skLineSegment(sketch, "E15.9.7.3", {"start": v(129.2, 63) * mm, "end": v(144.7, 63) * mm});
            skLineSegment(sketch, "E15.0.7.4", {"start": v(129.2, 98) * mm, "end": v(129.2, 82) * mm});
            skLineSegment(sketch, "E15.3.7.4", {"start": v(144.7, 98) * mm, "end": v(144.7, 82) * mm});
            skLineSegment(sketch, "E15.6.7.4", {"start": v(129.2, 98) * mm, "end": v(144.7, 98) * mm});
            skLineSegment(sketch, "E15.9.7.4", {"start": v(129.2, 82) * mm, "end": v(144.7, 82) * mm});
            skLineSegment(sketch, "E15.0.7.5", {"start": v(129.2, 117) * mm, "end": v(129.2, 101) * mm});
            skLineSegment(sketch, "E15.3.7.5", {"start": v(144.7, 117) * mm, "end": v(144.7, 101) * mm});
            skLineSegment(sketch, "E15.6.7.5", {"start": v(129.2, 117) * mm, "end": v(144.7, 117) * mm});
            skLineSegment(sketch, "E15.9.7.5", {"start": v(129.2, 101) * mm, "end": v(144.7, 101) * mm});
            skLineSegment(sketch, "E15.0.8.0", {"start": v(146.8, 22) * mm, "end": v(146.8, 6) * mm});
            skLineSegment(sketch, "E15.3.8.0", {"start": v(162.3, 22) * mm, "end": v(162.3, 6) * mm});
            skLineSegment(sketch, "E15.6.8.0", {"start": v(146.8, 22) * mm, "end": v(162.3, 22) * mm});
            skLineSegment(sketch, "E15.9.8.0", {"start": v(146.8, 6) * mm, "end": v(162.3, 6) * mm});
            skLineSegment(sketch, "E15.0.8.1", {"start": v(146.8, 41) * mm, "end": v(146.8, 25) * mm});
            skLineSegment(sketch, "E15.3.8.1", {"start": v(162.3, 41) * mm, "end": v(162.3, 25) * mm});
            skLineSegment(sketch, "E15.6.8.1", {"start": v(146.8, 41) * mm, "end": v(162.3, 41) * mm});
            skLineSegment(sketch, "E15.9.8.1", {"start": v(146.8, 25) * mm, "end": v(162.3, 25) * mm});
            skLineSegment(sketch, "E15.0.8.2", {"start": v(146.8, 60) * mm, "end": v(146.8, 44) * mm});
            skLineSegment(sketch, "E15.3.8.2", {"start": v(162.3, 60) * mm, "end": v(162.3, 44) * mm});
            skLineSegment(sketch, "E15.6.8.2", {"start": v(146.8, 60) * mm, "end": v(162.3, 60) * mm});
            skLineSegment(sketch, "E15.9.8.2", {"start": v(146.8, 44) * mm, "end": v(162.3, 44) * mm});
            skLineSegment(sketch, "E15.0.8.3", {"start": v(146.8, 79) * mm, "end": v(146.8, 63) * mm});
            skLineSegment(sketch, "E15.3.8.3", {"start": v(162.3, 79) * mm, "end": v(162.3, 63) * mm});
            skLineSegment(sketch, "E15.6.8.3", {"start": v(146.8, 79) * mm, "end": v(162.3, 79) * mm});
            skLineSegment(sketch, "E15.9.8.3", {"start": v(146.8, 63) * mm, "end": v(162.3, 63) * mm});
            skLineSegment(sketch, "E15.0.8.4", {"start": v(146.8, 98) * mm, "end": v(146.8, 82) * mm});
            skLineSegment(sketch, "E15.3.8.4", {"start": v(162.3, 98) * mm, "end": v(162.3, 82) * mm});
            skLineSegment(sketch, "E15.6.8.4", {"start": v(146.8, 98) * mm, "end": v(162.3, 98) * mm});
            skLineSegment(sketch, "E15.9.8.4", {"start": v(146.8, 82) * mm, "end": v(162.3, 82) * mm});
            skLineSegment(sketch, "E15.0.8.5", {"start": v(146.8, 117) * mm, "end": v(146.8, 101) * mm});
            skLineSegment(sketch, "E15.3.8.5", {"start": v(162.3, 117) * mm, "end": v(162.3, 101) * mm});
            skLineSegment(sketch, "E15.6.8.5", {"start": v(146.8, 117) * mm, "end": v(162.3, 117) * mm});
            skLineSegment(sketch, "E15.9.8.5", {"start": v(146.8, 101) * mm, "end": v(162.3, 101) * mm});
            skSolve(sketch);
        }
        {
            var Q0;
            Q0=qSketchRegion(id+"F9",true);
            extrude(context, id + "F10", {"entities" : qUnion([Q0]), "operationType" : NewBodyOperationType.REMOVE, "oppositeDirection" : true, "depth" : 140 * mm, "offsetDistance" : 25 * mm});
        }
        {
            var Q0;
            Q0=makeQuery(id+"F1.opExtrude","SWEPT_FACE",FACE,{"disambiguationData":[OSD([sQuery(id+"F0.wireOp",EDGE,"E0.right")])]});
            var sketch = newSketch(context, id + "F11", { "sketchPlane" : qUnion([Q0])});
            skLineSegment(sketch, "E16.bottom", {"start": v(49, 130) * mm, "end": v(91, 130) * mm});
            skLineSegment(sketch, "E16.top", {"start": v(49, 83) * mm, "end": v(91, 83) * mm});
            skLineSegment(sketch, "E16.left", {"start": v(49, 130) * mm, "end": v(49, 83) * mm});
            skLineSegment(sketch, "E16.right", {"start": v(91, 130) * mm, "end": v(91, 83) * mm});
            skSolve(sketch);
        }
        {
            var Q0;
            Q0=qSketchRegion(id+"F11",true);
            extrude(context, id + "F12", {"entities" : qUnion([Q0]), "operationType" : NewBodyOperationType.ADD, "oppositeDirection" : true, "depth" : 3 * mm, "offsetDistance" : 25 * mm});
        }
        {
            var Q0;
            Q0=makeQuery(id+"F1.opExtrude","SWEPT_FACE",FACE,{"disambiguationData":[OSD([sQuery(id+"F0.wireOp",EDGE,"E0.left")])]});
            var sketch = newSketch(context, id + "F13", { "sketchPlane" : qUnion([Q0])});
            skLineSegment(sketch, "E17.bottom", {"start": v(-91, 130) * mm, "end": v(-49, 130) * mm});
            skLineSegment(sketch, "E17.top", {"start": v(-91, 83) * mm, "end": v(-49, 83) * mm});
            skLineSegment(sketch, "E17.left", {"start": v(-91, 130) * mm, "end": v(-91, 83) * mm});
            skLineSegment(sketch, "E17.right", {"start": v(-49, 130) * mm, "end": v(-49, 83) * mm});
            skSolve(sketch);
        }
        {
            var Q0;
            Q0=qSketchRegion(id+"F13",true);
            extrude(context, id + "F14", {"entities" : qUnion([Q0]), "operationType" : NewBodyOperationType.ADD, "oppositeDirection" : true, "depth" : 3 * mm, "offsetDistance" : 25 * mm});
        }
        {
            var Q0;
            Q0=makeQuery(id+"F12.boolean.opBoolean","MERGE",FACE,{"derivedFrom":[makeQuery(id+"F1.opExtrude","SWEPT_FACE",FACE,{"disambiguationData":[OSD([sQuery(id+"F0.wireOp",EDGE,"E0.right")])]}),makeQuery(id+"F12.opExtrude","CAP_FACE",FACE,{"disambiguationData":[OSD([sQuery(id+"F11.wireOp",EDGE,"E16.bottom"),sQuery(id+"F11.wireOp",EDGE,"E16.top"),sQuery(id+"F11.wireOp",EDGE,"E16.left"),sQuery(id+"F11.wireOp",EDGE,"E16.right")])],"isStart":true})]});
            var sketch = newSketch(context, id + "F15", { "sketchPlane" : qUnion([Q0])});
            skLineSegment(sketch, "E18", {"start": v(70, 130) * mm, "end": v(71.4, -15.45) * mm, "construction": true});
            skCircle(sketch, "E19", {"center": v(80.14, 115) * mm, "radius": 4 * mm});
            skCircle(sketch, "E20", {"center": v(60.34, 95) * mm, "radius": 4 * mm});
            skSolve(sketch);
        }
        {
            var Q0;
            Q0=qSketchRegion(id+"F15",true);
            extrude(context, id + "F16", {"entities" : qUnion([Q0]), "operationType" : NewBodyOperationType.REMOVE, "oppositeDirection" : true, "depth" : 5 * mm, "offsetDistance" : 25 * mm});
        }
        {
            var Q0;
            Q0=makeQuery(id+"F14.boolean.opBoolean","MERGE",FACE,{"derivedFrom":[makeQuery(id+"F1.opExtrude","SWEPT_FACE",FACE,{"disambiguationData":[OSD([sQuery(id+"F0.wireOp",EDGE,"E0.left")])]}),makeQuery(id+"F14.opExtrude","CAP_FACE",FACE,{"disambiguationData":[OSD([sQuery(id+"F13.wireOp",EDGE,"E17.bottom"),sQuery(id+"F13.wireOp",EDGE,"E17.top"),sQuery(id+"F13.wireOp",EDGE,"E17.left"),sQuery(id+"F13.wireOp",EDGE,"E17.right")])],"isStart":true})]});
            var sketch = newSketch(context, id + "F17", { "sketchPlane" : qUnion([Q0])});
            skLineSegment(sketch, "E21", {"start": v(-70, 130) * mm, "end": v(-70, -4.6) * mm, "construction": true});
            skPoint(sketch, "E21.endSnap0", {"position": v(-70, 36) * mm});
            skCircle(sketch, "E22", {"center": v(-60, 115) * mm, "radius": 4 * mm});
            skCircle(sketch, "E23", {"center": v(-80, 95) * mm, "radius": 4 * mm});
            skSolve(sketch);
        }
        {
            var Q0;
            Q0=qSketchRegion(id+"F17",true);
            extrude(context, id + "F18", {"entities" : qUnion([Q0]), "operationType" : NewBodyOperationType.REMOVE, "oppositeDirection" : true, "depth" : 5 * mm, "offsetDistance" : 25 * mm});
        }
    });
